FCSTD DOCUMENT  (FreeCAD 0.19R19093 (Git))
Label: switchplate
License: All rights reserved
LicenseURL: http://en.wikipedia.org/wiki/All_rights_reserved
objects: Sketcher::SketchObject×1
note: 1 computed .brp shape members not serialized (recipe doc carries the construction recipe); baked Part::Feature solids carry a one-line shape summary decoded from their .brp

FEATURE [Sketcher::SketchObject] Sketch
  sketch-geometry (1004):
    g0: LineSegment [constr] StartX=-133.598 StartY=68.4339 StartZ=0 EndX=-114.548 EndY=68.4339 EndZ=0
    g1: LineSegment [constr] StartX=-114.548 StartY=68.4339 StartZ=0 EndX=-114.548 EndY=49.3839 EndZ=0
    g2: LineSegment [constr] StartX=-114.548 StartY=49.3839 StartZ=0 EndX=-133.598 EndY=49.3839 EndZ=0
    g3: LineSegment [constr] StartX=-133.598 StartY=49.3839 StartZ=0 EndX=-133.598 EndY=68.4339 EndZ=0
    g4: LineSegment [constr] StartX=-128.836 StartY=68.4339 StartZ=0 EndX=-128.836 EndY=49.3839 EndZ=0
    g5: LineSegment [constr] StartX=-124.073 StartY=68.4339 StartZ=0 EndX=-124.073 EndY=49.3839 EndZ=0
    g6: LineSegment [constr] StartX=-119.311 StartY=68.4339 StartZ=0 EndX=-119.311 EndY=49.3839 EndZ=0
    g7: LineSegment StartX=-131.073 StartY=65.9089 StartZ=0 EndX=-117.073 EndY=65.9089 EndZ=0
    g8: LineSegment StartX=-117.073 StartY=65.9089 StartZ=0 EndX=-117.073 EndY=51.9089 EndZ=0
    g9: LineSegment StartX=-117.073 StartY=51.9089 StartZ=0 EndX=-131.073 EndY=51.9089 EndZ=0
    g10: LineSegment StartX=-131.073 StartY=51.9089 StartZ=0 EndX=-131.073 EndY=65.9089 EndZ=0
    g11: LineSegment [constr] StartX=-129.78 StartY=36.1937 StartZ=0 EndX=-110.73 EndY=36.1937 EndZ=0
    g12: LineSegment [constr] StartX=-110.73 StartY=36.1937 StartZ=0 EndX=-110.73 EndY=17.1437 EndZ=0
    g13: LineSegment [constr] StartX=-110.73 StartY=17.1437 StartZ=0 EndX=-129.78 EndY=17.1437 EndZ=0
    g14: LineSegment [constr] StartX=-129.78 StartY=17.1437 StartZ=0 EndX=-129.78 EndY=36.1937 EndZ=0
    g15: LineSegment [constr] StartX=-125.018 StartY=36.1937 StartZ=0 EndX=-125.018 EndY=17.1437 EndZ=0
    g16: LineSegment [constr] StartX=-120.255 StartY=36.1937 StartZ=0 EndX=-120.255 EndY=17.1437 EndZ=0
    g17: LineSegment [constr] StartX=-115.493 StartY=36.1937 StartZ=0 EndX=-115.493 EndY=17.1437 EndZ=0
    g18: LineSegment [constr] StartX=-110.73 StartY=36.1937 StartZ=0 EndX=-105.968 EndY=36.1937 EndZ=0
    g19: LineSegment [constr] StartX=-105.968 StartY=36.1937 StartZ=0 EndX=-105.968 EndY=17.1437 EndZ=0
    g20: LineSegment [constr] StartX=-105.968 StartY=17.1437 StartZ=0 EndX=-110.73 EndY=17.1437 EndZ=0
    g21: LineSegment [constr] StartX=-117.874 StartY=36.1937 StartZ=0 EndX=-117.874 EndY=17.1437 EndZ=0
    g22: LineSegment StartX=-124.874 StartY=33.6687 StartZ=0 EndX=-110.874 EndY=33.6687 EndZ=0
    g23: LineSegment StartX=-110.874 StartY=33.6687 StartZ=0 EndX=-110.874 EndY=19.6687 EndZ=0
    g24: LineSegment StartX=-110.874 StartY=19.6687 StartZ=0 EndX=-124.874 EndY=19.6687 EndZ=0
    g25: LineSegment StartX=-124.874 StartY=19.6687 StartZ=0 EndX=-124.874 EndY=33.6687 EndZ=0
    g26: GeomPoint X=-117.874 Y=33.6687 Z=0
    g27: LineSegment [constr] StartX=-130.97 StartY=2.89697 StartZ=0 EndX=-111.92 EndY=2.89697 EndZ=0
    g28: LineSegment [constr] StartX=-111.92 StartY=2.89697 StartZ=0 EndX=-111.92 EndY=-16.153 EndZ=0
    g29: LineSegment [constr] StartX=-111.92 StartY=-16.153 StartZ=0 EndX=-130.97 EndY=-16.153 EndZ=0
    g30: LineSegment [constr] StartX=-130.97 StartY=-16.153 StartZ=0 EndX=-130.97 EndY=2.89697 EndZ=0
    g31: LineSegment [constr] StartX=-126.208 StartY=2.89697 StartZ=0 EndX=-126.208 EndY=-16.153 EndZ=0
    g32: LineSegment [constr] StartX=-121.445 StartY=2.89697 StartZ=0 EndX=-121.445 EndY=-16.153 EndZ=0
    g33: LineSegment [constr] StartX=-116.683 StartY=2.89697 StartZ=0 EndX=-116.683 EndY=-16.153 EndZ=0
    g34: LineSegment [constr] StartX=-111.92 StartY=2.89697 StartZ=0 EndX=-107.158 EndY=2.89697 EndZ=0
    g35: LineSegment [constr] StartX=-107.158 StartY=2.89697 StartZ=0 EndX=-107.158 EndY=-16.153 EndZ=0
    g36: LineSegment [constr] StartX=-107.158 StartY=-16.153 StartZ=0 EndX=-111.92 EndY=-16.153 EndZ=0
    g37: LineSegment [constr] StartX=-107.158 StartY=2.89697 StartZ=0 EndX=-102.395 EndY=2.89697 EndZ=0
    g38: LineSegment [constr] StartX=-102.395 StartY=2.89697 StartZ=0 EndX=-102.395 EndY=-16.153 EndZ=0
    g39: LineSegment [constr] StartX=-102.395 StartY=-16.153 StartZ=0 EndX=-107.158 EndY=-16.153 EndZ=0
    g40: LineSegment StartX=-123.683 StartY=0.371972 StartZ=0 EndX=-109.683 EndY=0.371972 EndZ=0
    g41: LineSegment StartX=-109.683 StartY=0.371972 StartZ=0 EndX=-109.683 EndY=-13.628 EndZ=0
    g42: LineSegment StartX=-109.683 StartY=-13.628 StartZ=0 EndX=-123.683 EndY=-13.628 EndZ=0
    g43: LineSegment StartX=-123.683 StartY=-13.628 StartZ=0 EndX=-123.683 EndY=0.371972 EndZ=0
    g44: GeomPoint X=-116.683 Y=0.371972 Z=0
    g45: LineSegment [constr] StartX=-131.666 StartY=-25.3858 StartZ=0 EndX=-112.616 EndY=-25.3858 EndZ=0
    g46: LineSegment [constr] StartX=-112.616 StartY=-25.3858 StartZ=0 EndX=-112.616 EndY=-44.4358 EndZ=0
    g47: LineSegment [constr] StartX=-112.616 StartY=-44.4358 StartZ=0 EndX=-131.666 EndY=-44.4358 EndZ=0
    g48: LineSegment [constr] StartX=-131.666 StartY=-44.4358 StartZ=0 EndX=-131.666 EndY=-25.3858 EndZ=0
    g49: LineSegment [constr] StartX=-126.903 StartY=-25.3858 StartZ=0 EndX=-126.903 EndY=-44.4358 EndZ=0
    g50: LineSegment [constr] StartX=-122.141 StartY=-25.3858 StartZ=0 EndX=-122.141 EndY=-44.4358 EndZ=0
    g51: LineSegment [constr] StartX=-117.378 StartY=-25.3858 StartZ=0 EndX=-117.378 EndY=-44.4358 EndZ=0
    g52: LineSegment [constr] StartX=-112.616 StartY=-25.3858 StartZ=0 EndX=-107.853 EndY=-25.3858 EndZ=0
    g53: LineSegment [constr] StartX=-107.853 StartY=-25.3858 StartZ=0 EndX=-107.853 EndY=-44.4358 EndZ=0
    g54: LineSegment [constr] StartX=-107.853 StartY=-44.4358 StartZ=0 EndX=-112.616 EndY=-44.4358 EndZ=0
    g55: LineSegment [constr] StartX=-107.853 StartY=-25.3858 StartZ=0 EndX=-103.091 EndY=-25.3858 EndZ=0
    g56: LineSegment [constr] StartX=-103.091 StartY=-25.3858 StartZ=0 EndX=-103.091 EndY=-44.4358 EndZ=0
    g57: LineSegment [constr] StartX=-103.091 StartY=-44.4358 StartZ=0 EndX=-107.853 EndY=-44.4358 EndZ=0
    g58: LineSegment [constr] StartX=-103.091 StartY=-25.3858 StartZ=0 EndX=-98.3281 EndY=-25.3858 EndZ=0
    g59: LineSegment [constr] StartX=-98.3281 StartY=-25.3858 StartZ=0 EndX=-98.3281 EndY=-44.4358 EndZ=0
    g60: LineSegment [constr] StartX=-98.3281 StartY=-44.4358 StartZ=0 EndX=-103.091 EndY=-44.4358 EndZ=0
    g61: LineSegment [constr] StartX=-114.997 StartY=-25.3858 StartZ=0 EndX=-114.997 EndY=-44.4358 EndZ=0
    g62: LineSegment StartX=-121.997 StartY=-27.9108 StartZ=0 EndX=-107.997 EndY=-27.9108 EndZ=0
    g63: LineSegment StartX=-107.997 StartY=-27.9108 StartZ=0 EndX=-107.997 EndY=-41.9108 EndZ=0
    g64: LineSegment StartX=-107.997 StartY=-41.9108 StartZ=0 EndX=-121.997 EndY=-41.9108 EndZ=0
    g65: LineSegment StartX=-121.997 StartY=-41.9108 StartZ=0 EndX=-121.997 EndY=-27.9108 EndZ=0
    g66: GeomPoint X=-114.997 Y=-27.9108 Z=0
    g67: LineSegment [constr] StartX=-133.994 StartY=-54.7146 StartZ=0 EndX=-114.944 EndY=-54.7146 EndZ=0
    g68: LineSegment [constr] StartX=-114.944 StartY=-54.7146 StartZ=0 EndX=-114.944 EndY=-73.7646 EndZ=0
    g69: LineSegment [constr] StartX=-114.944 StartY=-73.7646 StartZ=0 EndX=-133.994 EndY=-73.7646 EndZ=0
    g70: LineSegment [constr] StartX=-133.994 StartY=-73.7646 StartZ=0 EndX=-133.994 EndY=-54.7146 EndZ=0
    g71: LineSegment [constr] StartX=-129.232 StartY=-54.7146 StartZ=0 EndX=-129.232 EndY=-73.7646 EndZ=0
    g72: LineSegment [constr] StartX=-124.469 StartY=-54.7146 StartZ=0 EndX=-124.469 EndY=-73.7646 EndZ=0
    g73: LineSegment [constr] StartX=-119.707 StartY=-54.7146 StartZ=0 EndX=-119.707 EndY=-73.7646 EndZ=0
    g74: LineSegment [constr] StartX=-114.944 StartY=-54.7146 StartZ=0 EndX=-110.182 EndY=-54.7146 EndZ=0
    g75: LineSegment [constr] StartX=-110.182 StartY=-54.7146 StartZ=0 EndX=-110.182 EndY=-73.7646 EndZ=0
    g76: LineSegment [constr] StartX=-110.182 StartY=-73.7646 StartZ=0 EndX=-114.944 EndY=-73.7646 EndZ=0
    g77: LineSegment [constr] StartX=-110.182 StartY=-54.7146 StartZ=0 EndX=-105.419 EndY=-54.7146 EndZ=0
    g78: LineSegment [constr] StartX=-105.419 StartY=-54.7146 StartZ=0 EndX=-105.419 EndY=-73.7646 EndZ=0
    g79: LineSegment [constr] StartX=-105.419 StartY=-73.7646 StartZ=0 EndX=-110.182 EndY=-73.7646 EndZ=0
    g80: LineSegment [constr] StartX=-105.419 StartY=-54.7146 StartZ=0 EndX=-100.657 EndY=-54.7146 EndZ=0
    g81: LineSegment [constr] StartX=-100.657 StartY=-54.7146 StartZ=0 EndX=-100.657 EndY=-73.7646 EndZ=0
    g82: LineSegment [constr] StartX=-100.657 StartY=-73.7646 StartZ=0 EndX=-105.419 EndY=-73.7646 EndZ=0
    g83: LineSegment [constr] StartX=-100.657 StartY=-54.7146 StartZ=0 EndX=-95.8941 EndY=-54.7146 EndZ=0
    g84: LineSegment [constr] StartX=-95.8941 StartY=-54.7146 StartZ=0 EndX=-95.8941 EndY=-73.7646 EndZ=0
    g85: LineSegment [constr] StartX=-95.8941 StartY=-73.7646 StartZ=0 EndX=-100.657 EndY=-73.7646 EndZ=0
    g86: LineSegment StartX=-121.944 StartY=-57.2396 StartZ=0 EndX=-107.944 EndY=-57.2396 EndZ=0
    g87: LineSegment StartX=-107.944 StartY=-57.2396 StartZ=0 EndX=-107.944 EndY=-71.2396 EndZ=0
    g88: LineSegment StartX=-107.944 StartY=-71.2396 StartZ=0 EndX=-121.944 EndY=-71.2396 EndZ=0
    g89: LineSegment StartX=-121.944 StartY=-71.2396 StartZ=0 EndX=-121.944 EndY=-57.2396 EndZ=0
    g90: GeomPoint X=-114.944 Y=-57.2396 Z=0
    g91: LineSegment [constr] StartX=-133.693 StartY=-86.5988 StartZ=0 EndX=-114.643 EndY=-86.5988 EndZ=0
    g92: LineSegment [constr] StartX=-114.643 StartY=-86.5988 StartZ=0 EndX=-114.643 EndY=-105.649 EndZ=0
    g93: LineSegment [constr] StartX=-114.643 StartY=-105.649 StartZ=0 EndX=-133.693 EndY=-105.649 EndZ=0
    g94: LineSegment [constr] StartX=-133.693 StartY=-105.649 StartZ=0 EndX=-133.693 EndY=-86.5988 EndZ=0
    g95: LineSegment [constr] StartX=-128.93 StartY=-86.5988 StartZ=0 EndX=-128.93 EndY=-105.649 EndZ=0
    g96: LineSegment [constr] StartX=-124.168 StartY=-86.5988 StartZ=0 EndX=-124.168 EndY=-105.649 EndZ=0
    g97: LineSegment [constr] StartX=-119.405 StartY=-86.5988 StartZ=0 EndX=-119.405 EndY=-105.649 EndZ=0
    g98: LineSegment [constr] StartX=-114.643 StartY=-86.5988 StartZ=0 EndX=-109.88 EndY=-86.5988 EndZ=0
    g99: LineSegment [constr] StartX=-109.88 StartY=-86.5988 StartZ=0 EndX=-109.88 EndY=-105.649 EndZ=0
    g100: LineSegment [constr] StartX=-109.88 StartY=-105.649 StartZ=0 EndX=-114.643 EndY=-105.649 EndZ=0
    g101: LineSegment [constr] StartX=-109.88 StartY=-86.5988 StartZ=0 EndX=-105.118 EndY=-86.5988 EndZ=0
    g102: LineSegment [constr] StartX=-105.118 StartY=-86.5988 StartZ=0 EndX=-105.118 EndY=-105.649 EndZ=0
    g103: LineSegment [constr] StartX=-105.118 StartY=-105.649 StartZ=0 EndX=-109.88 EndY=-105.649 EndZ=0
    g104: LineSegment [constr] StartX=-105.118 StartY=-86.5988 StartZ=0 EndX=-100.355 EndY=-86.5988 EndZ=0
    g105: LineSegment [constr] StartX=-100.355 StartY=-86.5988 StartZ=0 EndX=-100.355 EndY=-105.649 EndZ=0
    g106: LineSegment [constr] StartX=-100.355 StartY=-105.649 StartZ=0 EndX=-105.118 EndY=-105.649 EndZ=0
    g107: LineSegment [constr] StartX=-100.355 StartY=-86.5988 StartZ=0 EndX=-95.5928 EndY=-86.5988 EndZ=0
    g108: LineSegment [constr] StartX=-95.5928 StartY=-86.5988 StartZ=0 EndX=-95.5928 EndY=-105.649 EndZ=0
    g109: LineSegment [constr] StartX=-95.5928 StartY=-105.649 StartZ=0 EndX=-100.355 EndY=-105.649 EndZ=0
    g110: LineSegment [constr] StartX=-95.5928 StartY=-86.5988 StartZ=0 EndX=-90.8303 EndY=-86.5988 EndZ=0
    g111: LineSegment [constr] StartX=-90.8303 StartY=-86.5988 StartZ=0 EndX=-90.8303 EndY=-105.649 EndZ=0
    g112: LineSegment [constr] StartX=-90.8303 StartY=-105.649 StartZ=0 EndX=-95.5928 EndY=-105.649 EndZ=0
    g113: LineSegment [constr] StartX=-112.262 StartY=-86.5988 StartZ=0 EndX=-112.262 EndY=-105.649 EndZ=0
    g114: GeomPoint X=-112.262 Y=-89.1238 Z=0
    g115: LineSegment StartX=-119.262 StartY=-89.1238 StartZ=0 EndX=-105.262 EndY=-89.1238 EndZ=0
    g116: LineSegment StartX=-105.262 StartY=-89.1238 StartZ=0 EndX=-105.262 EndY=-103.124 EndZ=0
    g117: LineSegment StartX=-105.262 StartY=-103.124 StartZ=0 EndX=-119.262 EndY=-103.124 EndZ=0
    g118: LineSegment StartX=-119.262 StartY=-103.124 StartZ=0 EndX=-119.262 EndY=-89.1238 EndZ=0
    g119: LineSegment [constr] StartX=-64.4313 StartY=98.9607 StartZ=0 EndX=-45.3813 EndY=98.9607 EndZ=0
    g120: LineSegment [constr] StartX=-45.3813 StartY=98.9607 StartZ=0 EndX=-45.3813 EndY=79.9107 EndZ=0
    g121: LineSegment [constr] StartX=-45.3813 StartY=79.9107 StartZ=0 EndX=-64.4313 EndY=79.9107 EndZ=0
    g122: LineSegment [constr] StartX=-64.4313 StartY=79.9107 StartZ=0 EndX=-64.4313 EndY=98.9607 EndZ=0
    g123: LineSegment [constr] StartX=-59.6688 StartY=98.9607 StartZ=0 EndX=-59.6688 EndY=79.9107 EndZ=0
    g124: LineSegment [constr] StartX=-54.9063 StartY=98.9607 StartZ=0 EndX=-54.9063 EndY=79.9107 EndZ=0
    g125: LineSegment [constr] StartX=-50.1438 StartY=98.9607 StartZ=0 EndX=-50.1438 EndY=79.9107 EndZ=0
    g126: LineSegment StartX=-61.9063 StartY=96.4357 StartZ=0 EndX=-47.9063 EndY=96.4357 EndZ=0
    g127: LineSegment StartX=-47.9063 StartY=96.4357 StartZ=0 EndX=-47.9063 EndY=82.4357 EndZ=0
    g128: LineSegment StartX=-47.9063 StartY=82.4357 StartZ=0 EndX=-61.9063 EndY=82.4357 EndZ=0
    g129: LineSegment StartX=-61.9063 StartY=82.4357 StartZ=0 EndX=-61.9063 EndY=96.4357 EndZ=0
    g130: LineSegment [constr] StartX=-35.8563 StartY=98.9607 StartZ=0 EndX=-16.8063 EndY=98.9607 EndZ=0
    g131: LineSegment [constr] StartX=-16.8063 StartY=98.9607 StartZ=0 EndX=-16.8063 EndY=79.9107 EndZ=0
    g132: LineSegment [constr] StartX=-16.8063 StartY=79.9107 StartZ=0 EndX=-35.8563 EndY=79.9107 EndZ=0
    g133: LineSegment [constr] StartX=-35.8563 StartY=79.9107 StartZ=0 EndX=-35.8563 EndY=98.9607 EndZ=0
    g134: LineSegment [constr] StartX=-31.0938 StartY=98.9607 StartZ=0 EndX=-31.0938 EndY=79.9107 EndZ=0
    g135: LineSegment [constr] StartX=-26.3313 StartY=98.9607 StartZ=0 EndX=-26.3313 EndY=79.9107 EndZ=0
    g136: LineSegment [constr] StartX=-21.5688 StartY=98.9607 StartZ=0 EndX=-21.5688 EndY=79.9107 EndZ=0
    g137: LineSegment StartX=-33.3313 StartY=96.4357 StartZ=0 EndX=-19.3313 EndY=96.4357 EndZ=0
    g138: LineSegment StartX=-19.3313 StartY=96.4357 StartZ=0 EndX=-19.3313 EndY=82.4357 EndZ=0
    g139: LineSegment StartX=-19.3313 StartY=82.4357 StartZ=0 EndX=-33.3313 EndY=82.4357 EndZ=0
    g140: LineSegment StartX=-33.3313 StartY=82.4357 StartZ=0 EndX=-33.3313 EndY=96.4357 EndZ=0
    g141: LineSegment [constr] StartX=-16.8063 StartY=98.9607 StartZ=0 EndX=2.24369 EndY=98.9607 EndZ=0
    g142: LineSegment [constr] StartX=2.24369 StartY=98.9607 StartZ=0 EndX=2.24369 EndY=79.9107 EndZ=0
    g143: LineSegment [constr] StartX=2.24369 StartY=79.9107 StartZ=0 EndX=-16.8063 EndY=79.9107 EndZ=0
    g144: LineSegment [constr] StartX=-16.8063 StartY=79.9107 StartZ=0 EndX=-16.8063 EndY=98.9607 EndZ=0
    g145: LineSegment [constr] StartX=-12.0438 StartY=98.9607 StartZ=0 EndX=-12.0438 EndY=79.9107 EndZ=0
    g146: LineSegment [constr] StartX=-7.28131 StartY=98.9607 StartZ=0 EndX=-7.28131 EndY=79.9107 EndZ=0
    g147: LineSegment [constr] StartX=-2.51881 StartY=98.9607 StartZ=0 EndX=-2.51881 EndY=79.9107 EndZ=0
    g148: LineSegment StartX=-14.2813 StartY=96.4357 StartZ=0 EndX=-0.28131 EndY=96.4357 EndZ=0
    g149: LineSegment StartX=-0.28131 StartY=96.4357 StartZ=0 EndX=-0.28131 EndY=82.4357 EndZ=0
    g150: LineSegment StartX=-0.28131 StartY=82.4357 StartZ=0 EndX=-14.2813 EndY=82.4357 EndZ=0
    g151: LineSegment StartX=-14.2813 StartY=82.4357 StartZ=0 EndX=-14.2813 EndY=96.4357 EndZ=0
    g152: LineSegment [constr] StartX=2.24369 StartY=98.9607 StartZ=0 EndX=21.2937 EndY=98.9607 EndZ=0
    g153: LineSegment [constr] StartX=21.2937 StartY=98.9607 StartZ=0 EndX=21.2937 EndY=79.9107 EndZ=0
    g154: LineSegment [constr] StartX=21.2937 StartY=79.9107 StartZ=0 EndX=2.24369 EndY=79.9107 EndZ=0
    g155: LineSegment [constr] StartX=2.24369 StartY=79.9107 StartZ=0 EndX=2.24369 EndY=98.9607 EndZ=0
    g156: LineSegment [constr] StartX=7.00619 StartY=98.9607 StartZ=0 EndX=7.00619 EndY=79.9107 EndZ=0
    g157: LineSegment [constr] StartX=11.7687 StartY=98.9607 StartZ=0 EndX=11.7687 EndY=79.9107 EndZ=0
    g158: LineSegment [constr] StartX=16.5312 StartY=98.9607 StartZ=0 EndX=16.5312 EndY=79.9107 EndZ=0
    g159: LineSegment StartX=4.76869 StartY=96.4357 StartZ=0 EndX=18.7687 EndY=96.4357 EndZ=0
    g160: LineSegment StartX=18.7687 StartY=96.4357 StartZ=0 EndX=18.7687 EndY=82.4357 EndZ=0
    g161: LineSegment StartX=18.7687 StartY=82.4357 StartZ=0 EndX=4.76869 EndY=82.4357 EndZ=0
    g162: LineSegment StartX=4.76869 StartY=82.4357 StartZ=0 EndX=4.76869 EndY=96.4357 EndZ=0
    g163: LineSegment [constr] StartX=21.2937 StartY=98.9607 StartZ=0 EndX=40.3437 EndY=98.9607 EndZ=0
    g164: LineSegment [constr] StartX=40.3437 StartY=98.9607 StartZ=0 EndX=40.3437 EndY=79.9107 EndZ=0
    g165: LineSegment [constr] StartX=40.3437 StartY=79.9107 StartZ=0 EndX=21.2937 EndY=79.9107 EndZ=0
    g166: LineSegment [constr] StartX=21.2937 StartY=79.9107 StartZ=0 EndX=21.2937 EndY=98.9607 EndZ=0
    g167: LineSegment [constr] StartX=26.0562 StartY=98.9607 StartZ=0 EndX=26.0562 EndY=79.9107 EndZ=0
    g168: LineSegment [constr] StartX=30.8187 StartY=98.9607 StartZ=0 EndX=30.8187 EndY=79.9107 EndZ=0
    g169: LineSegment [constr] StartX=35.5812 StartY=98.9607 StartZ=0 EndX=35.5812 EndY=79.9107 EndZ=0
    g170: LineSegment StartX=23.8187 StartY=96.4357 StartZ=0 EndX=37.8187 EndY=96.4357 EndZ=0
    g171: LineSegment StartX=37.8187 StartY=96.4357 StartZ=0 EndX=37.8187 EndY=82.4357 EndZ=0
    g172: LineSegment StartX=37.8187 StartY=82.4357 StartZ=0 EndX=23.8187 EndY=82.4357 EndZ=0
    g173: LineSegment StartX=23.8187 StartY=82.4357 StartZ=0 EndX=23.8187 EndY=96.4357 EndZ=0
    g174: LineSegment [constr] StartX=54.6312 StartY=98.9607 StartZ=0 EndX=73.6812 EndY=98.9607 EndZ=0
    g175: LineSegment [constr] StartX=73.6812 StartY=98.9607 StartZ=0 EndX=73.6812 EndY=79.9107 EndZ=0
    g176: LineSegment [constr] StartX=73.6812 StartY=79.9107 StartZ=0 EndX=54.6312 EndY=79.9107 EndZ=0
    g177: LineSegment [constr] StartX=54.6312 StartY=79.9107 StartZ=0 EndX=54.6312 EndY=98.9607 EndZ=0
    g178: LineSegment [constr] StartX=59.3937 StartY=98.9607 StartZ=0 EndX=59.3937 EndY=79.9107 EndZ=0
    g179: LineSegment [constr] StartX=64.1562 StartY=98.9607 StartZ=0 EndX=64.1562 EndY=79.9107 EndZ=0
    g180: LineSegment [constr] StartX=68.9187 StartY=98.9607 StartZ=0 EndX=68.9187 EndY=79.9107 EndZ=0
    g181: LineSegment StartX=57.1562 StartY=96.4357 StartZ=0 EndX=71.1562 EndY=96.4357 EndZ=0
    g182: LineSegment StartX=71.1562 StartY=96.4357 StartZ=0 EndX=71.1562 EndY=82.4357 EndZ=0
    g183: LineSegment StartX=71.1562 StartY=82.4357 StartZ=0 EndX=57.1562 EndY=82.4357 EndZ=0
    g184: LineSegment StartX=57.1562 StartY=82.4357 StartZ=0 EndX=57.1562 EndY=96.4357 EndZ=0
    g185: LineSegment [constr] StartX=73.6812 StartY=98.9607 StartZ=0 EndX=92.7312 EndY=98.9607 EndZ=0
    g186: LineSegment [constr] StartX=92.7312 StartY=98.9607 StartZ=0 EndX=92.7312 EndY=79.9107 EndZ=0
    g187: LineSegment [constr] StartX=92.7312 StartY=79.9107 StartZ=0 EndX=73.6812 EndY=79.9107 EndZ=0
    g188: LineSegment [constr] StartX=73.6812 StartY=79.9107 StartZ=0 EndX=73.6812 EndY=98.9607 EndZ=0
    g189: LineSegment [constr] StartX=78.4437 StartY=98.9607 StartZ=0 EndX=78.4437 EndY=79.9107 EndZ=0
    g190: LineSegment [constr] StartX=83.2062 StartY=98.9607 StartZ=0 EndX=83.2062 EndY=79.9107 EndZ=0
    g191: LineSegment [constr] StartX=87.9687 StartY=98.9607 StartZ=0 EndX=87.9687 EndY=79.9107 EndZ=0
    g192: LineSegment StartX=76.2062 StartY=96.4357 StartZ=0 EndX=90.2062 EndY=96.4357 EndZ=0
    g193: LineSegment StartX=90.2062 StartY=96.4357 StartZ=0 EndX=90.2062 EndY=82.4357 EndZ=0
    g194: LineSegment StartX=90.2062 StartY=82.4357 StartZ=0 EndX=76.2062 EndY=82.4357 EndZ=0
    g195: LineSegment StartX=76.2062 StartY=82.4357 StartZ=0 EndX=76.2062 EndY=96.4357 EndZ=0
    g196: LineSegment [constr] StartX=92.7312 StartY=98.9607 StartZ=0 EndX=111.781 EndY=98.9607 EndZ=0
    g197: LineSegment [constr] StartX=111.781 StartY=98.9607 StartZ=0 EndX=111.781 EndY=79.9107 EndZ=0
    g198: LineSegment [constr] StartX=111.781 StartY=79.9107 StartZ=0 EndX=92.7312 EndY=79.9107 EndZ=0
    g199: LineSegment [constr] StartX=92.7312 StartY=79.9107 StartZ=0 EndX=92.7312 EndY=98.9607 EndZ=0
    g200: LineSegment [constr] StartX=97.4937 StartY=98.9607 StartZ=0 EndX=97.4937 EndY=79.9107 EndZ=0
    g201: LineSegment [constr] StartX=102.256 StartY=98.9607 StartZ=0 EndX=102.256 EndY=79.9107 EndZ=0
    g202: LineSegment [constr] StartX=107.019 StartY=98.9607 StartZ=0 EndX=107.019 EndY=79.9107 EndZ=0
    g203: LineSegment StartX=95.2562 StartY=96.4357 StartZ=0 EndX=109.256 EndY=96.4357 EndZ=0
    g204: LineSegment StartX=109.256 StartY=96.4357 StartZ=0 EndX=109.256 EndY=82.4357 EndZ=0
    g205: LineSegment StartX=109.256 StartY=82.4357 StartZ=0 EndX=95.2562 EndY=82.4357 EndZ=0
    g206: LineSegment StartX=95.2562 StartY=82.4357 StartZ=0 EndX=95.2562 EndY=96.4357 EndZ=0
    g207: LineSegment [constr] StartX=111.781 StartY=98.9607 StartZ=0 EndX=130.831 EndY=98.9607 EndZ=0
    g208: LineSegment [constr] StartX=130.831 StartY=98.9607 StartZ=0 EndX=130.831 EndY=79.9107 EndZ=0
    g209: LineSegment [constr] StartX=130.831 StartY=79.9107 StartZ=0 EndX=111.781 EndY=79.9107 EndZ=0
    g210: LineSegment [constr] StartX=111.781 StartY=79.9107 StartZ=0 EndX=111.781 EndY=98.9607 EndZ=0
    g211: LineSegment [constr] StartX=116.544 StartY=98.9607 StartZ=0 EndX=116.544 EndY=79.9107 EndZ=0
    g212: LineSegment [constr] StartX=121.306 StartY=98.9607 StartZ=0 EndX=121.306 EndY=79.9107 EndZ=0
    g213: LineSegment [constr] StartX=126.069 StartY=98.9607 StartZ=0 EndX=126.069 EndY=79.9107 EndZ=0
    g214: LineSegment StartX=114.306 StartY=96.4357 StartZ=0 EndX=128.306 EndY=96.4357 EndZ=0
    g215: LineSegment StartX=128.306 StartY=96.4357 StartZ=0 EndX=128.306 EndY=82.4357 EndZ=0
    g216: LineSegment StartX=128.306 StartY=82.4357 StartZ=0 EndX=114.306 EndY=82.4357 EndZ=0
    g217: LineSegment StartX=114.306 StartY=82.4357 StartZ=0 EndX=114.306 EndY=96.4357 EndZ=0
    g218: LineSegment [constr] StartX=145.119 StartY=98.9607 StartZ=0 EndX=164.169 EndY=98.9607 EndZ=0
    g219: LineSegment [constr] StartX=164.169 StartY=98.9607 StartZ=0 EndX=164.169 EndY=79.9107 EndZ=0
    g220: LineSegment [constr] StartX=164.169 StartY=79.9107 StartZ=0 EndX=145.119 EndY=79.9107 EndZ=0
    g221: LineSegment [constr] StartX=145.119 StartY=79.9107 StartZ=0 EndX=145.119 EndY=98.9607 EndZ=0
    g222: LineSegment [constr] StartX=149.881 StartY=98.9607 StartZ=0 EndX=149.881 EndY=79.9107 EndZ=0
    g223: LineSegment [constr] StartX=154.644 StartY=98.9607 StartZ=0 EndX=154.644 EndY=79.9107 EndZ=0
    g224: LineSegment [constr] StartX=159.406 StartY=98.9607 StartZ=0 EndX=159.406 EndY=79.9107 EndZ=0
    g225: LineSegment StartX=147.644 StartY=96.4357 StartZ=0 EndX=161.644 EndY=96.4357 EndZ=0
    g226: LineSegment StartX=161.644 StartY=96.4357 StartZ=0 EndX=161.644 EndY=82.4357 EndZ=0
    g227: LineSegment StartX=161.644 StartY=82.4357 StartZ=0 EndX=147.644 EndY=82.4357 EndZ=0
    g228: LineSegment StartX=147.644 StartY=82.4357 StartZ=0 EndX=147.644 EndY=96.4357 EndZ=0
    g229: LineSegment [constr] StartX=164.169 StartY=98.9607 StartZ=0 EndX=183.219 EndY=98.9607 EndZ=0
    g230: LineSegment [constr] StartX=183.219 StartY=98.9607 StartZ=0 EndX=183.219 EndY=79.9107 EndZ=0
    g231: LineSegment [constr] StartX=183.219 StartY=79.9107 StartZ=0 EndX=164.169 EndY=79.9107 EndZ=0
    g232: LineSegment [constr] StartX=164.169 StartY=79.9107 StartZ=0 EndX=164.169 EndY=98.9607 EndZ=0
    g233: LineSegment [constr] StartX=168.931 StartY=98.9607 StartZ=0 EndX=168.931 EndY=79.9107 EndZ=0
    g234: LineSegment [constr] StartX=173.694 StartY=98.9607 StartZ=0 EndX=173.694 EndY=79.9107 EndZ=0
    g235: LineSegment [constr] StartX=178.456 StartY=98.9607 StartZ=0 EndX=178.456 EndY=79.9107 EndZ=0
    g236: LineSegment StartX=166.694 StartY=96.4357 StartZ=0 EndX=180.694 EndY=96.4357 EndZ=0
    g237: LineSegment StartX=180.694 StartY=96.4357 StartZ=0 EndX=180.694 EndY=82.4357 EndZ=0
    g238: LineSegment StartX=180.694 StartY=82.4357 StartZ=0 EndX=166.694 EndY=82.4357 EndZ=0
    g239: LineSegment StartX=166.694 StartY=82.4357 StartZ=0 EndX=166.694 EndY=96.4357 EndZ=0
    g240: LineSegment [constr] StartX=183.219 StartY=98.9607 StartZ=0 EndX=202.269 EndY=98.9607 EndZ=0
    g241: LineSegment [constr] StartX=202.269 StartY=98.9607 StartZ=0 EndX=202.269 EndY=79.9107 EndZ=0
    g242: LineSegment [constr] StartX=202.269 StartY=79.9107 StartZ=0 EndX=183.219 EndY=79.9107 EndZ=0
    g243: LineSegment [constr] StartX=183.219 StartY=79.9107 StartZ=0 EndX=183.219 EndY=98.9607 EndZ=0
    g244: LineSegment [constr] StartX=187.981 StartY=98.9607 StartZ=0 EndX=187.981 EndY=79.9107 EndZ=0
    g245: LineSegment [constr] StartX=192.744 StartY=98.9607 StartZ=0 EndX=192.744 EndY=79.9107 EndZ=0
    g246: LineSegment [constr] StartX=197.506 StartY=98.9607 StartZ=0 EndX=197.506 EndY=79.9107 EndZ=0
    g247: LineSegment StartX=185.744 StartY=96.4357 StartZ=0 EndX=199.744 EndY=96.4357 EndZ=0
    g248: LineSegment StartX=199.744 StartY=96.4357 StartZ=0 EndX=199.744 EndY=82.4357 EndZ=0
    g249: LineSegment StartX=199.744 StartY=82.4357 StartZ=0 EndX=185.744 EndY=82.4357 EndZ=0
    g250: LineSegment StartX=185.744 StartY=82.4357 StartZ=0 EndX=185.744 EndY=96.4357 EndZ=0
    g251: LineSegment [constr] StartX=202.269 StartY=98.9607 StartZ=0 EndX=221.319 EndY=98.9607 EndZ=0
    g252: LineSegment [constr] StartX=221.319 StartY=98.9607 StartZ=0 EndX=221.319 EndY=79.9107 EndZ=0
    g253: LineSegment [constr] StartX=221.319 StartY=79.9107 StartZ=0 EndX=202.269 EndY=79.9107 EndZ=0
    g254: LineSegment [constr] StartX=202.269 StartY=79.9107 StartZ=0 EndX=202.269 EndY=98.9607 EndZ=0
    g255: LineSegment [constr] StartX=207.031 StartY=98.9607 StartZ=0 EndX=207.031 EndY=79.9107 EndZ=0
    g256: LineSegment [constr] StartX=211.794 StartY=98.9607 StartZ=0 EndX=211.794 EndY=79.9107 EndZ=0
    g257: LineSegment [constr] StartX=216.556 StartY=98.9607 StartZ=0 EndX=216.556 EndY=79.9107 EndZ=0
    g258: LineSegment StartX=204.794 StartY=96.4357 StartZ=0 EndX=218.794 EndY=96.4357 EndZ=0
    g259: LineSegment StartX=218.794 StartY=96.4357 StartZ=0 EndX=218.794 EndY=82.4357 EndZ=0
    g260: LineSegment StartX=218.794 StartY=82.4357 StartZ=0 EndX=204.794 EndY=82.4357 EndZ=0
    g261: LineSegment StartX=204.794 StartY=82.4357 StartZ=0 EndX=204.794 EndY=96.4357 EndZ=0
    g262: LineSegment [constr] StartX=228.106 StartY=99.0816 StartZ=0 EndX=247.156 EndY=99.0816 EndZ=0
    g263: LineSegment [constr] StartX=247.156 StartY=99.0816 StartZ=0 EndX=247.156 EndY=80.0316 EndZ=0
    g264: LineSegment [constr] StartX=247.156 StartY=80.0316 StartZ=0 EndX=228.106 EndY=80.0316 EndZ=0
    g265: LineSegment [constr] StartX=228.106 StartY=80.0316 StartZ=0 EndX=228.106 EndY=99.0816 EndZ=0
    g266: LineSegment [constr] StartX=232.869 StartY=99.0816 StartZ=0 EndX=232.869 EndY=80.0316 EndZ=0
    g267: LineSegment [constr] StartX=237.631 StartY=99.0816 StartZ=0 EndX=237.631 EndY=80.0316 EndZ=0
    g268: LineSegment [constr] StartX=242.394 StartY=99.0816 StartZ=0 EndX=242.394 EndY=80.0316 EndZ=0
    g269: LineSegment StartX=230.631 StartY=96.5566 StartZ=0 EndX=244.631 EndY=96.5566 EndZ=0
    g270: LineSegment StartX=244.631 StartY=96.5566 StartZ=0 EndX=244.631 EndY=82.5566 EndZ=0
    g271: LineSegment StartX=244.631 StartY=82.5566 StartZ=0 EndX=230.631 EndY=82.5566 EndZ=0
    g272: LineSegment StartX=230.631 StartY=82.5566 StartZ=0 EndX=230.631 EndY=96.5566 EndZ=0
    g273: LineSegment [constr] StartX=228.106 StartY=89.5566 StartZ=0 EndX=247.156 EndY=89.5566 EndZ=0
    g274: GeomPoint X=237.631 Y=89.5566 Z=0
    g275: LineSegment [constr] StartX=-64.4313 StartY=72.7682 StartZ=0 EndX=-45.3813 EndY=72.7682 EndZ=0
    g276: LineSegment [constr] StartX=-45.3813 StartY=72.7682 StartZ=0 EndX=-45.3813 EndY=53.7182 EndZ=0
    g277: LineSegment [constr] StartX=-45.3813 StartY=53.7182 StartZ=0 EndX=-64.4313 EndY=53.7182 EndZ=0
    g278: LineSegment [constr] StartX=-64.4313 StartY=53.7182 StartZ=0 EndX=-64.4313 EndY=72.7682 EndZ=0
    g279: LineSegment [constr] StartX=-59.6688 StartY=72.7682 StartZ=0 EndX=-59.6688 EndY=53.7182 EndZ=0
    g280: LineSegment [constr] StartX=-54.9063 StartY=72.7682 StartZ=0 EndX=-54.9063 EndY=53.7182 EndZ=0
    g281: LineSegment [constr] StartX=-50.1438 StartY=72.7682 StartZ=0 EndX=-50.1438 EndY=53.7182 EndZ=0
    g282: LineSegment StartX=-61.9063 StartY=70.2432 StartZ=0 EndX=-47.9063 EndY=70.2432 EndZ=0
    g283: LineSegment StartX=-47.9063 StartY=70.2432 StartZ=0 EndX=-47.9063 EndY=56.2432 EndZ=0
    g284: LineSegment StartX=-47.9063 StartY=56.2432 StartZ=0 EndX=-61.9063 EndY=56.2432 EndZ=0
    g285: LineSegment StartX=-61.9063 StartY=56.2432 StartZ=0 EndX=-61.9063 EndY=70.2432 EndZ=0
    g286: LineSegment [constr] StartX=-45.3813 StartY=72.7682 StartZ=0 EndX=-26.3313 EndY=72.7682 EndZ=0
    g287: LineSegment [constr] StartX=-26.3313 StartY=72.7682 StartZ=0 EndX=-26.3313 EndY=53.7182 EndZ=0
    g288: LineSegment [constr] StartX=-26.3313 StartY=53.7182 StartZ=0 EndX=-45.3813 EndY=53.7182 EndZ=0
    g289: LineSegment [constr] StartX=-45.3813 StartY=53.7182 StartZ=0 EndX=-45.3813 EndY=72.7682 EndZ=0
    g290: LineSegment [constr] StartX=-40.6188 StartY=72.7682 StartZ=0 EndX=-40.6188 EndY=53.7182 EndZ=0
    g291: LineSegment [constr] StartX=-35.8563 StartY=72.7682 StartZ=0 EndX=-35.8563 EndY=53.7182 EndZ=0
    g292: LineSegment [constr] StartX=-31.0938 StartY=72.7682 StartZ=0 EndX=-31.0938 EndY=53.7182 EndZ=0
    g293: LineSegment StartX=-42.8563 StartY=70.2432 StartZ=0 EndX=-28.8563 EndY=70.2432 EndZ=0
    g294: LineSegment StartX=-28.8563 StartY=70.2432 StartZ=0 EndX=-28.8563 EndY=56.2432 EndZ=0
    g295: LineSegment StartX=-28.8563 StartY=56.2432 StartZ=0 EndX=-42.8563 EndY=56.2432 EndZ=0
    g296: LineSegment StartX=-42.8563 StartY=56.2432 StartZ=0 EndX=-42.8563 EndY=70.2432 EndZ=0
    g297: LineSegment [constr] StartX=-26.3313 StartY=72.7682 StartZ=0 EndX=-7.28131 EndY=72.7682 EndZ=0
    g298: LineSegment [constr] StartX=-7.28131 StartY=72.7682 StartZ=0 EndX=-7.28131 EndY=53.7182 EndZ=0
    g299: LineSegment [constr] StartX=-7.28131 StartY=53.7182 StartZ=0 EndX=-26.3313 EndY=53.7182 EndZ=0
    g300: LineSegment [constr] StartX=-26.3313 StartY=53.7182 StartZ=0 EndX=-26.3313 EndY=72.7682 EndZ=0
    g301: LineSegment [constr] StartX=-21.5688 StartY=72.7682 StartZ=0 EndX=-21.5688 EndY=53.7182 EndZ=0
    g302: LineSegment [constr] StartX=-16.8063 StartY=72.7682 StartZ=0 EndX=-16.8063 EndY=53.7182 EndZ=0
    g303: LineSegment [constr] StartX=-12.0438 StartY=72.7682 StartZ=0 EndX=-12.0438 EndY=53.7182 EndZ=0
    g304: LineSegment StartX=-23.8063 StartY=70.2432 StartZ=0 EndX=-9.80631 EndY=70.2432 EndZ=0
    g305: LineSegment StartX=-9.80631 StartY=70.2432 StartZ=0 EndX=-9.80631 EndY=56.2432 EndZ=0
    g306: LineSegment StartX=-9.80631 StartY=56.2432 StartZ=0 EndX=-23.8063 EndY=56.2432 EndZ=0
    g307: LineSegment StartX=-23.8063 StartY=56.2432 StartZ=0 EndX=-23.8063 EndY=70.2432 EndZ=0
    g308: LineSegment [constr] StartX=-7.28131 StartY=72.7682 StartZ=0 EndX=11.7687 EndY=72.7682 EndZ=0
    g309: LineSegment [constr] StartX=11.7687 StartY=72.7682 StartZ=0 EndX=11.7687 EndY=53.7182 EndZ=0
    g310: LineSegment [constr] StartX=11.7687 StartY=53.7182 StartZ=0 EndX=-7.28131 EndY=53.7182 EndZ=0
    g311: LineSegment [constr] StartX=-7.28131 StartY=53.7182 StartZ=0 EndX=-7.28131 EndY=72.7682 EndZ=0
    g312: LineSegment [constr] StartX=-2.51881 StartY=72.7682 StartZ=0 EndX=-2.51881 EndY=53.7182 EndZ=0
    g313: LineSegment [constr] StartX=2.24369 StartY=72.7682 StartZ=0 EndX=2.24369 EndY=53.7182 EndZ=0
    g314: LineSegment [constr] StartX=7.00619 StartY=72.7682 StartZ=0 EndX=7.00619 EndY=53.7182 EndZ=0
    g315: LineSegment StartX=-4.75631 StartY=70.2432 StartZ=0 EndX=9.24369 EndY=70.2432 EndZ=0
    g316: LineSegment StartX=9.24369 StartY=70.2432 StartZ=0 EndX=9.24369 EndY=56.2432 EndZ=0
    g317: LineSegment StartX=9.24369 StartY=56.2432 StartZ=0 EndX=-4.75631 EndY=56.2432 EndZ=0
    g318: LineSegment StartX=-4.75631 StartY=56.2432 StartZ=0 EndX=-4.75631 EndY=70.2432 EndZ=0
    g319: LineSegment [constr] StartX=11.7687 StartY=72.7682 StartZ=0 EndX=30.8187 EndY=72.7682 EndZ=0
    g320: LineSegment [constr] StartX=30.8187 StartY=72.7682 StartZ=0 EndX=30.8187 EndY=53.7182 EndZ=0
    g321: LineSegment [constr] StartX=30.8187 StartY=53.7182 StartZ=0 EndX=11.7687 EndY=53.7182 EndZ=0
    g322: LineSegment [constr] StartX=11.7687 StartY=53.7182 StartZ=0 EndX=11.7687 EndY=72.7682 EndZ=0
    g323: LineSegment [constr] StartX=16.5312 StartY=72.7682 StartZ=0 EndX=16.5312 EndY=53.7182 EndZ=0
    g324: LineSegment [constr] StartX=21.2937 StartY=72.7682 StartZ=0 EndX=21.2937 EndY=53.7182 EndZ=0
    g325: LineSegment [constr] StartX=26.0562 StartY=72.7682 StartZ=0 EndX=26.0562 EndY=53.7182 EndZ=0
    g326: LineSegment StartX=14.2937 StartY=70.2432 StartZ=0 EndX=28.2937 EndY=70.2432 EndZ=0
    g327: LineSegment StartX=28.2937 StartY=70.2432 StartZ=0 EndX=28.2937 EndY=56.2432 EndZ=0
    g328: LineSegment StartX=28.2937 StartY=56.2432 StartZ=0 EndX=14.2937 EndY=56.2432 EndZ=0
    g329: LineSegment StartX=14.2937 StartY=56.2432 StartZ=0 EndX=14.2937 EndY=70.2432 EndZ=0
    g330: LineSegment [constr] StartX=30.8187 StartY=72.7682 StartZ=0 EndX=49.8687 EndY=72.7682 EndZ=0
    g331: LineSegment [constr] StartX=49.8687 StartY=72.7682 StartZ=0 EndX=49.8687 EndY=53.7182 EndZ=0
    g332: LineSegment [constr] StartX=49.8687 StartY=53.7182 StartZ=0 EndX=30.8187 EndY=53.7182 EndZ=0
    g333: LineSegment [constr] StartX=30.8187 StartY=53.7182 StartZ=0 EndX=30.8187 EndY=72.7682 EndZ=0
    g334: LineSegment [constr] StartX=35.5812 StartY=72.7682 StartZ=0 EndX=35.5812 EndY=53.7182 EndZ=0
    g335: LineSegment [constr] StartX=40.3437 StartY=72.7682 StartZ=0 EndX=40.3437 EndY=53.7182 EndZ=0
    g336: LineSegment [constr] StartX=45.1062 StartY=72.7682 StartZ=0 EndX=45.1062 EndY=53.7182 EndZ=0
    g337: LineSegment StartX=33.3437 StartY=70.2432 StartZ=0 EndX=47.3437 EndY=70.2432 EndZ=0
    g338: LineSegment StartX=47.3437 StartY=70.2432 StartZ=0 EndX=47.3437 EndY=56.2432 EndZ=0
    g339: LineSegment StartX=47.3437 StartY=56.2432 StartZ=0 EndX=33.3437 EndY=56.2432 EndZ=0
    g340: LineSegment StartX=33.3437 StartY=56.2432 StartZ=0 EndX=33.3437 EndY=70.2432 EndZ=0
    g341: LineSegment [constr] StartX=49.8687 StartY=72.7682 StartZ=0 EndX=68.9187 EndY=72.7682 EndZ=0
    g342: LineSegment [constr] StartX=68.9187 StartY=72.7682 StartZ=0 EndX=68.9187 EndY=53.7182 EndZ=0
    g343: LineSegment [constr] StartX=68.9187 StartY=53.7182 StartZ=0 EndX=49.8687 EndY=53.7182 EndZ=0
    g344: LineSegment [constr] StartX=49.8687 StartY=53.7182 StartZ=0 EndX=49.8687 EndY=72.7682 EndZ=0
    g345: LineSegment [constr] StartX=54.6312 StartY=72.7682 StartZ=0 EndX=54.6312 EndY=53.7182 EndZ=0
    g346: LineSegment [constr] StartX=59.3937 StartY=72.7682 StartZ=0 EndX=59.3937 EndY=53.7182 EndZ=0
    g347: LineSegment [constr] StartX=64.1562 StartY=72.7682 StartZ=0 EndX=64.1562 EndY=53.7182 EndZ=0
    g348: LineSegment StartX=52.3937 StartY=70.2432 StartZ=0 EndX=66.3937 EndY=70.2432 EndZ=0
    g349: LineSegment StartX=66.3937 StartY=70.2432 StartZ=0 EndX=66.3937 EndY=56.2432 EndZ=0
    g350: LineSegment StartX=66.3937 StartY=56.2432 StartZ=0 EndX=52.3937 EndY=56.2432 EndZ=0
    g351: LineSegment StartX=52.3937 StartY=56.2432 StartZ=0 EndX=52.3937 EndY=70.2432 EndZ=0
    g352: LineSegment [constr] StartX=68.9187 StartY=72.7682 StartZ=0 EndX=87.9687 EndY=72.7682 EndZ=0
    g353: LineSegment [constr] StartX=87.9687 StartY=72.7682 StartZ=0 EndX=87.9687 EndY=53.7182 EndZ=0
    g354: LineSegment [constr] StartX=87.9687 StartY=53.7182 StartZ=0 EndX=68.9187 EndY=53.7182 EndZ=0
    g355: LineSegment [constr] StartX=68.9187 StartY=53.7182 StartZ=0 EndX=68.9187 EndY=72.7682 EndZ=0
    g356: LineSegment [constr] StartX=73.6812 StartY=72.7682 StartZ=0 EndX=73.6812 EndY=53.7182 EndZ=0
    g357: LineSegment [constr] StartX=78.4437 StartY=72.7682 StartZ=0 EndX=78.4437 EndY=53.7182 EndZ=0
    g358: LineSegment [constr] StartX=83.2062 StartY=72.7682 StartZ=0 EndX=83.2062 EndY=53.7182 EndZ=0
    g359: LineSegment StartX=71.4437 StartY=70.2432 StartZ=0 EndX=85.4437 EndY=70.2432 EndZ=0
    g360: LineSegment StartX=85.4437 StartY=70.2432 StartZ=0 EndX=85.4437 EndY=56.2432 EndZ=0
    g361: LineSegment StartX=85.4437 StartY=56.2432 StartZ=0 EndX=71.4437 EndY=56.2432 EndZ=0
    g362: LineSegment StartX=71.4437 StartY=56.2432 StartZ=0 EndX=71.4437 EndY=70.2432 EndZ=0
    g363: LineSegment [constr] StartX=87.9687 StartY=72.7682 StartZ=0 EndX=107.019 EndY=72.7682 EndZ=0
    g364: LineSegment [constr] StartX=107.019 StartY=72.7682 StartZ=0 EndX=107.019 EndY=53.7182 EndZ=0
    g365: LineSegment [constr] StartX=107.019 StartY=53.7182 StartZ=0 EndX=87.9687 EndY=53.7182 EndZ=0
    g366: LineSegment [constr] StartX=87.9687 StartY=53.7182 StartZ=0 EndX=87.9687 EndY=72.7682 EndZ=0
    g367: LineSegment [constr] StartX=92.7312 StartY=72.7682 StartZ=0 EndX=92.7312 EndY=53.7182 EndZ=0
    g368: LineSegment [constr] StartX=97.4937 StartY=72.7682 StartZ=0 EndX=97.4937 EndY=53.7182 EndZ=0
    g369: LineSegment [constr] StartX=102.256 StartY=72.7682 StartZ=0 EndX=102.256 EndY=53.7182 EndZ=0
    g370: LineSegment StartX=90.4937 StartY=70.2432 StartZ=0 EndX=104.494 EndY=70.2432 EndZ=0
    g371: LineSegment StartX=104.494 StartY=70.2432 StartZ=0 EndX=104.494 EndY=56.2432 EndZ=0
    g372: LineSegment StartX=104.494 StartY=56.2432 StartZ=0 EndX=90.4937 EndY=56.2432 EndZ=0
    g373: LineSegment StartX=90.4937 StartY=56.2432 StartZ=0 EndX=90.4937 EndY=70.2432 EndZ=0
    g374: LineSegment [constr] StartX=107.019 StartY=72.7682 StartZ=0 EndX=126.069 EndY=72.7682 EndZ=0
    g375: LineSegment [constr] StartX=126.069 StartY=72.7682 StartZ=0 EndX=126.069 EndY=53.7182 EndZ=0
    g376: LineSegment [constr] StartX=126.069 StartY=53.7182 StartZ=0 EndX=107.019 EndY=53.7182 EndZ=0
    g377: LineSegment [constr] StartX=107.019 StartY=53.7182 StartZ=0 EndX=107.019 EndY=72.7682 EndZ=0
    g378: LineSegment [constr] StartX=111.781 StartY=72.7682 StartZ=0 EndX=111.781 EndY=53.7182 EndZ=0
    g379: LineSegment [constr] StartX=116.544 StartY=72.7682 StartZ=0 EndX=116.544 EndY=53.7182 EndZ=0
    g380: LineSegment [constr] StartX=121.306 StartY=72.7682 StartZ=0 EndX=121.306 EndY=53.7182 EndZ=0
    g381: LineSegment StartX=109.544 StartY=70.2432 StartZ=0 EndX=123.544 EndY=70.2432 EndZ=0
    g382: LineSegment StartX=123.544 StartY=70.2432 StartZ=0 EndX=123.544 EndY=56.2432 EndZ=0
    g383: LineSegment StartX=123.544 StartY=56.2432 StartZ=0 EndX=109.544 EndY=56.2432 EndZ=0
    g384: LineSegment StartX=109.544 StartY=56.2432 StartZ=0 EndX=109.544 EndY=70.2432 EndZ=0
    g385: LineSegment [constr] StartX=126.069 StartY=72.7682 StartZ=0 EndX=145.119 EndY=72.7682 EndZ=0
    g386: LineSegment [constr] StartX=145.119 StartY=72.7682 StartZ=0 EndX=145.119 EndY=53.7182 EndZ=0
    g387: LineSegment [constr] StartX=145.119 StartY=53.7182 StartZ=0 EndX=126.069 EndY=53.7182 EndZ=0
    g388: LineSegment [constr] StartX=126.069 StartY=53.7182 StartZ=0 EndX=126.069 EndY=72.7682 EndZ=0
    g389: LineSegment [constr] StartX=130.831 StartY=72.7682 StartZ=0 EndX=130.831 EndY=53.7182 EndZ=0
    g390: LineSegment [constr] StartX=135.594 StartY=72.7682 StartZ=0 EndX=135.594 EndY=53.7182 EndZ=0
    g391: LineSegment [constr] StartX=140.356 StartY=72.7682 StartZ=0 EndX=140.356 EndY=53.7182 EndZ=0
    g392: LineSegment StartX=128.594 StartY=70.2432 StartZ=0 EndX=142.594 EndY=70.2432 EndZ=0
    g393: LineSegment StartX=142.594 StartY=70.2432 StartZ=0 EndX=142.594 EndY=56.2432 EndZ=0
    g394: LineSegment StartX=142.594 StartY=56.2432 StartZ=0 EndX=128.594 EndY=56.2432 EndZ=0
    g395: LineSegment StartX=128.594 StartY=56.2432 StartZ=0 EndX=128.594 EndY=70.2432 EndZ=0
    g396: LineSegment [constr] StartX=145.119 StartY=72.7682 StartZ=0 EndX=164.169 EndY=72.7682 EndZ=0
    g397: LineSegment [constr] StartX=164.169 StartY=72.7682 StartZ=0 EndX=164.169 EndY=53.7182 EndZ=0
    g398: LineSegment [constr] StartX=164.169 StartY=53.7182 StartZ=0 EndX=145.119 EndY=53.7182 EndZ=0
    g399: LineSegment [constr] StartX=145.119 StartY=53.7182 StartZ=0 EndX=145.119 EndY=72.7682 EndZ=0
    ... +604 more geometry lines
  constraints (2836):
    c: Coincident(g0,g1)
    c: Coincident(g1,g2)
    c: Coincident(g2,g3)
    c: Coincident(g3,g0)
    c: Horizontal(g0)
    c: Horizontal(g2)
    c: Vertical(g1)
    c: Vertical(g3)
    c: PointOnObject(g4,g2)
    c: PointOnObject(g5,g2)
    c: PointOnObject(g6,g2)
    c: Vertical(g6)
    c: Vertical(g4)
    c: Vertical(g5)
    c: Symmetric(g0,g0,g5)
    c: Symmetric(g0,g5,g4)
    c: Symmetric(g5,g0,g6)
    c: DistanceX(g0,g0) = 19.05
    c: DistanceY(g3,g3) = 19.05
    c: Coincident(g7,g8)
    c: Coincident(g8,g9)
    c: Coincident(g9,g10)
    c: Coincident(g10,g7)
    c: Horizontal(g7)
    c: Horizontal(g9)
    c: Vertical(g8)
    c: Vertical(g10)
    c: DistanceX(g7,g7) = 14
    c: DistanceY(g10,g10) = 14
    c: DistanceY(g7,g0) = 2.525
    c: DistanceX(g0,g7) = 2.525
    c: Coincident(g11,g12)
    c: Coincident(g12,g13)
    c: Coincident(g13,g14)
    c: Coincident(g14,g11)
    c: Horizontal(g11)
    c: Horizontal(g13)
    c: Vertical(g12)
    c: Vertical(g14)
    c: PointOnObject(g15,g13)
    c: PointOnObject(g16,g13)
    c: PointOnObject(g17,g13)
    c: Vertical(g17)
    c: Vertical(g15)
    c: Vertical(g16)
    c: Symmetric(g11,g11,g16)
    c: Symmetric(g11,g16,g15)
    c: Symmetric(g16,g11,g17)
    c: DistanceX(g11,g11) = 19.05
    c: DistanceY(g14,g14) = 19.05
    c: Coincident(g18,g11)
    c: Coincident(g19,g18)
    c: Vertical(g19)
    c: Coincident(g20,g19)
    c: Coincident(g20,g12)
    c: Horizontal(g20)
    c: PointOnObject(g21,g13)
    c: Vertical(g21)
    c: Symmetric(g16,g17,g21)
    c: Symmetric(g17,g18,g11)
    c: Coincident(g22,g23)
    c: Coincident(g23,g24)
    c: Coincident(g24,g25)
    c: Coincident(g25,g22)
    c: Horizontal(g22)
    c: Horizontal(g24)
    c: Vertical(g23)
    c: Vertical(g25)
    c: DistanceY(g25,g25) = 14
    c: DistanceX(g22,g22) = 14
    c: Symmetric(g22,g22,g26)
    c: PointOnObject(g26,g21)
    c: DistanceY(g26,g21) = 2.525
    c: Coincident(g27,g28)
    c: Coincident(g28,g29)
    c: Coincident(g29,g30)
    c: Coincident(g30,g27)
    c: Horizontal(g27)
    c: Horizontal(g29)
    c: Vertical(g28)
    c: Vertical(g30)
    c: PointOnObject(g31,g29)
    c: PointOnObject(g32,g29)
    c: PointOnObject(g33,g29)
    c: Vertical(g33)
    c: Vertical(g31)
    c: Vertical(g32)
    c: Symmetric(g27,g27,g32)
    c: Symmetric(g27,g32,g31)
    c: Symmetric(g32,g27,g33)
    c: DistanceX(g27,g27) = 19.05
    c: DistanceY(g30,g30) = 19.05
    c: Coincident(g34,g27)
    c: Coincident(g35,g34)
    c: Vertical(g35)
    c: Coincident(g36,g35)
    c: Coincident(g36,g28)
    c: Horizontal(g36)
    c: Symmetric(g33,g34,g27)
    c: Coincident(g37,g34)
    c: Vertical(g38)
    c: Coincident(g39,g38)
    c: Coincident(g39,g35)
    c: Horizontal(g39)
    c: Coincident(g38,g37)
    c: Symmetric(g27,g37,g34)
    c: Coincident(g40,g41)
    c: Coincident(g41,g42)
    c: Coincident(g42,g43)
    c: Coincident(g43,g40)
    c: Horizontal(g40)
    c: Horizontal(g42)
    c: Vertical(g41)
    c: Vertical(g43)
    c: DistanceX(g40,g40) = 14
    c: DistanceY(g43,g43) = 14
    c: PointOnObject(g44,g33)
    c: Symmetric(g40,g40,g44)
    c: DistanceY(g44,g33) = 2.525
    c: Coincident(g45,g46)
    c: Coincident(g46,g47)
    c: Coincident(g47,g48)
    c: Coincident(g48,g45)
    c: Horizontal(g45)
    c: Horizontal(g47)
    c: Vertical(g46)
    c: Vertical(g48)
    c: PointOnObject(g49,g47)
    c: PointOnObject(g50,g47)
    c: PointOnObject(g51,g47)
    c: Vertical(g51)
    c: Vertical(g49)
    c: Vertical(g50)
    c: Symmetric(g45,g45,g50)
    c: Symmetric(g45,g50,g49)
    c: Symmetric(g50,g45,g51)
    c: DistanceX(g45,g45) = 19.05
    c: DistanceY(g48,g48) = 19.05
    c: Coincident(g52,g45)
    c: Coincident(g53,g52)
    c: Vertical(g53)
    c: Coincident(g54,g53)
    c: Coincident(g54,g46)
    c: Horizontal(g54)
    c: Symmetric(g51,g52,g45)
    c: Coincident(g55,g52)
    c: Vertical(g56)
    c: Coincident(g57,g56)
    c: Coincident(g57,g53)
    c: Horizontal(g57)
    c: Coincident(g56,g55)
    c: Symmetric(g45,g55,g52)
    c: Coincident(g58,g55)
    c: Vertical(g59)
    c: Coincident(g60,g59)
    c: Coincident(g60,g56)
    c: Coincident(g58,g59)
    c: Horizontal(g60)
    c: Symmetric(g52,g58,g55)
    c: Vertical(g61)
    c: Symmetric(g51,g45,g61)
    c: Coincident(g62,g63)
    c: Coincident(g63,g64)
    c: Coincident(g64,g65)
    c: Coincident(g65,g62)
    c: Horizontal(g62)
    c: Horizontal(g64)
    c: Vertical(g63)
    c: Vertical(g65)
    c: DistanceX(g62,g62) = 14
    c: DistanceY(g65,g65) = 14
    c: Symmetric(g62,g62,g66)
    c: PointOnObject(g66,g61)
    c: DistanceY(g66,g61) = 2.525
    c: Coincident(g67,g68)
    c: Coincident(g68,g69)
    c: Coincident(g69,g70)
    c: Coincident(g70,g67)
    c: Horizontal(g67)
    c: Horizontal(g69)
    c: Vertical(g68)
    c: Vertical(g70)
    c: PointOnObject(g71,g69)
    c: PointOnObject(g72,g69)
    c: PointOnObject(g73,g69)
    c: Vertical(g73)
    c: Vertical(g71)
    c: Vertical(g72)
    c: Symmetric(g67,g67,g72)
    c: Symmetric(g67,g72,g71)
    c: Symmetric(g72,g67,g73)
    c: DistanceX(g67,g67) = 19.05
    c: DistanceY(g70,g70) = 19.05
    c: Coincident(g74,g67)
    c: Coincident(g75,g74)
    c: Vertical(g75)
    c: Coincident(g76,g75)
    c: Coincident(g76,g68)
    c: Horizontal(g76)
    c: Symmetric(g73,g74,g67)
    c: Coincident(g77,g74)
    c: Vertical(g78)
    c: Coincident(g79,g78)
    c: Coincident(g79,g75)
    c: Horizontal(g79)
    c: Coincident(g78,g77)
    c: Symmetric(g67,g77,g74)
    c: Coincident(g80,g77)
    c: Vertical(g81)
    c: Coincident(g82,g81)
    c: Coincident(g82,g78)
    c: Coincident(g80,g81)
    c: Horizontal(g82)
    c: Symmetric(g74,g80,g77)
    c: PointOnObject(g61,g47)
    c: Coincident(g83,g80)
    c: Coincident(g84,g83)
    c: Vertical(g84)
    c: Coincident(g85,g84)
    c: Coincident(g85,g81)
    c: Horizontal(g85)
    c: Symmetric(g77,g83,g80)
    c: Coincident(g86,g87)
    c: Coincident(g87,g88)
    c: Coincident(g88,g89)
    c: Coincident(g89,g86)
    c: Horizontal(g86)
    c: Horizontal(g88)
    c: Vertical(g87)
    c: Vertical(g89)
    c: DistanceY(g89,g89) = 14
    c: DistanceX(g86,g86) = 14
    c: Symmetric(g86,g86,g90)
    c: PointOnObject(g90,g68)
    c: DistanceY(g90,g67) = 2.525
    c: Coincident(g91,g92)
    c: Coincident(g92,g93)
    c: Coincident(g93,g94)
    c: Coincident(g94,g91)
    c: Horizontal(g91)
    c: Horizontal(g93)
    c: Vertical(g92)
    c: Vertical(g94)
    c: PointOnObject(g95,g93)
    c: PointOnObject(g96,g93)
    c: PointOnObject(g97,g93)
    c: Vertical(g97)
    c: Vertical(g95)
    c: Vertical(g96)
    c: Symmetric(g91,g91,g96)
    c: Symmetric(g91,g96,g95)
    c: Symmetric(g96,g91,g97)
    c: DistanceX(g91,g91) = 19.05
    c: DistanceY(g94,g94) = 19.05
    c: Coincident(g98,g91)
    c: Coincident(g99,g98)
    c: Vertical(g99)
    c: Coincident(g100,g99)
    c: Coincident(g100,g92)
    c: Horizontal(g100)
    c: Symmetric(g97,g98,g91)
    c: Coincident(g101,g98)
    c: Vertical(g102)
    c: Coincident(g103,g102)
    c: Coincident(g103,g99)
    c: Horizontal(g103)
    c: Coincident(g102,g101)
    c: Symmetric(g91,g101,g98)
    c: Coincident(g104,g101)
    c: Vertical(g105)
    c: Coincident(g106,g105)
    c: Coincident(g106,g102)
    c: Coincident(g104,g105)
    c: Horizontal(g106)
    c: Symmetric(g98,g104,g101)
    c: Coincident(g107,g104)
    c: Coincident(g108,g107)
    c: Vertical(g108)
    c: Coincident(g109,g108)
    c: Coincident(g109,g105)
    c: Horizontal(g109)
    c: Symmetric(g101,g107,g104)
    c: Coincident(g110,g107)
    c: Coincident(g111,g110)
    c: Vertical(g111)
    c: Coincident(g112,g111)
    c: Coincident(g112,g108)
    c: Horizontal(g112)
    c: Symmetric(g104,g110,g107)
    c: Vertical(g113)
    c: PointOnObject(g113,g100)
    c: Symmetric(g91,g98,g113)
    c: Coincident(g115,g116)
    c: Coincident(g116,g117)
    c: Coincident(g117,g118)
    c: Coincident(g118,g115)
    c: Horizontal(g115)
    c: Horizontal(g117)
    c: Vertical(g116)
    c: Vertical(g118)
    c: DistanceX(g115,g115) = 14
    c: DistanceY(g118,g118) = 14
    c: DistanceY(g114,g113) = 2.525
    c: Symmetric(g115,g115,g114)
    c: PointOnObject(g114,g113)
    c: Coincident(g119,g120)
    c: Coincident(g120,g121)
    c: Coincident(g121,g122)
    c: Coincident(g122,g119)
    c: Horizontal(g119)
    c: Horizontal(g121)
    c: Vertical(g120)
    c: Vertical(g122)
    c: PointOnObject(g123,g121)
    c: PointOnObject(g124,g121)
    c: PointOnObject(g125,g121)
    c: Vertical(g125)
    c: Vertical(g123)
    c: Vertical(g124)
    c: Symmetric(g119,g119,g124)
    c: Symmetric(g119,g124,g123)
    c: Symmetric(g124,g119,g125)
    c: DistanceX(g119,g119) = 19.05
    c: DistanceY(g122,g122) = 19.05
    c: Coincident(g126,g127)
    c: Coincident(g127,g128)
    c: Coincident(g128,g129)
    c: Coincident(g129,g126)
    c: Horizontal(g126)
    c: Horizontal(g128)
    c: Vertical(g127)
    c: Vertical(g129)
    c: DistanceX(g126,g126) = 14
    c: DistanceY(g129,g129) = 14
    c: DistanceY(g126,g119) = 2.525
    c: DistanceX(g119,g126) = 2.525
    c: Coincident(g130,g131)
    c: Coincident(g131,g132)
    c: Coincident(g132,g133)
    c: Coincident(g133,g130)
    c: Horizontal(g130)
    c: Horizontal(g132)
    c: Vertical(g131)
    c: Vertical(g133)
    c: PointOnObject(g134,g132)
    c: PointOnObject(g135,g132)
    c: PointOnObject(g136,g132)
    c: Vertical(g136)
    c: Vertical(g134)
    c: Vertical(g135)
    c: Symmetric(g130,g130,g135)
    c: Symmetric(g130,g135,g134)
    c: Symmetric(g135,g130,g136)
    c: DistanceX(g130,g130) = 19.05
    c: DistanceY(g133,g133) = 19.05
    c: Coincident(g137,g138)
    c: Coincident(g138,g139)
    c: Coincident(g139,g140)
    c: Coincident(g140,g137)
    c: Horizontal(g137)
    c: Horizontal(g139)
    c: Vertical(g138)
    c: Vertical(g140)
    c: DistanceX(g137,g137) = 14
    c: DistanceY(g140,g140) = 14
    c: DistanceY(g137,g130) = 2.525
    c: DistanceX(g130,g137) = 2.525
    c: DistanceX(g128,g139) = 28.575
    c: DistanceY(g139,g128) = 0
    c: Coincident(g141,g142)
    c: Coincident(g142,g143)
    c: Coincident(g143,g144)
    c: Coincident(g144,g141)
    c: Horizontal(g141)
    c: Horizontal(g143)
    c: Vertical(g142)
    c: Vertical(g144)
    c: PointOnObject(g145,g143)
    c: PointOnObject(g146,g143)
    c: PointOnObject(g147,g143)
    c: Vertical(g147)
    c: Vertical(g145)
    c: Vertical(g146)
    c: Symmetric(g141,g141,g146)
    c: Symmetric(g141,g146,g145)
    c: Symmetric(g146,g141,g147)
    c: DistanceX(g141,g141) = 19.05
    c: DistanceY(g144,g144) = 19.05
    c: Coincident(g148,g149)
    c: Coincident(g149,g150)
    c: Coincident(g150,g151)
    c: Coincident(g151,g148)
    c: Horizontal(g148)
    c: Horizontal(g150)
    c: Vertical(g149)
    c: Vertical(g151)
    c: DistanceX(g148,g148) = 14
    c: DistanceY(g151,g151) = 14
    c: DistanceY(g148,g141) = 2.525
    c: DistanceX(g141,g148) = 2.525
    c: Coincident(g143,g131)
    c: Coincident(g152,g153)
    c: Coincident(g153,g154)
    c: Coincident(g154,g155)
    c: Coincident(g155,g152)
    c: Horizontal(g152)
    c: Horizontal(g154)
    c: Vertical(g153)
    c: Vertical(g155)
    c: PointOnObject(g156,g154)
    c: PointOnObject(g157,g154)
    c: PointOnObject(g158,g154)
    c: Vertical(g158)
    c: Vertical(g156)
    c: Vertical(g157)
    c: Symmetric(g152,g152,g157)
    c: Symmetric(g152,g157,g156)
    c: Symmetric(g157,g152,g158)
    c: DistanceX(g152,g152) = 19.05
    c: DistanceY(g155,g155) = 19.05
    c: Coincident(g159,g160)
    c: Coincident(g160,g161)
    c: Coincident(g161,g162)
    c: Coincident(g162,g159)
    c: Horizontal(g159)
    c: Horizontal(g161)
    c: Vertical(g160)
    c: Vertical(g162)
    c: DistanceX(g159,g159) = 14
    c: DistanceY(g162,g162) = 14
    c: DistanceY(g159,g152) = 2.525
    c: DistanceX(g152,g159) = 2.525
    c: Coincident(g163,g164)
    c: Coincident(g164,g165)
    c: Coincident(g165,g166)
    c: Coincident(g166,g163)
    c: Horizontal(g163)
    c: Horizontal(g165)
    c: Vertical(g164)
    c: Vertical(g166)
    c: PointOnObject(g167,g165)
    c: PointOnObject(g168,g165)
    c: PointOnObject(g169,g165)
    c: Vertical(g169)
    c: Vertical(g167)
    c: Vertical(g168)
    c: Symmetric(g163,g163,g168)
    c: Symmetric(g163,g168,g167)
    c: Symmetric(g168,g163,g169)
    c: DistanceX(g163,g163) = 19.05
    c: DistanceY(g166,g166) = 19.05
    c: Coincident(g170,g171)
    c: Coincident(g171,g172)
    c: Coincident(g172,g173)
    c: Coincident(g173,g170)
    c: Horizontal(g170)
    c: Horizontal(g172)
    c: Vertical(g171)
    c: Vertical(g173)
    c: DistanceX(g170,g170) = 14
    c: DistanceY(g173,g173) = 14
    c: DistanceY(g170,g163) = 2.525
    c: DistanceX(g163,g170) = 2.525
    c: Coincident(g165,g153)
    c: Coincident(g154,g142)
    c: Coincident(g174,g175)
    c: Coincident(g175,g176)
    c: Coincident(g176,g177)
    c: Coincident(g177,g174)
    c: Horizontal(g174)
    c: Horizontal(g176)
    c: Vertical(g175)
    c: Vertical(g177)
    c: PointOnObject(g178,g176)
    c: PointOnObject(g179,g176)
    c: PointOnObject(g180,g176)
    c: Vertical(g180)
    c: Vertical(g178)
    c: Vertical(g179)
    c: Symmetric(g174,g174,g179)
    c: Symmetric(g174,g179,g178)
    c: Symmetric(g179,g174,g180)
    c: DistanceX(g174,g174) = 19.05
    c: DistanceY(g177,g177) = 19.05
    c: Coincident(g181,g182)
    c: Coincident(g182,g183)
    c: Coincident(g183,g184)
    c: Coincident(g184,g181)
    c: Horizontal(g181)
    c: Horizontal(g183)
    c: Vertical(g182)
    c: Vertical(g184)
    c: DistanceX(g181,g181) = 14
    c: DistanceY(g184,g184) = 14
    c: DistanceY(g181,g174) = 2.525
    c: DistanceX(g174,g181) = 2.525
    c: Coincident(g185,g186)
    c: Coincident(g186,g187)
    c: Coincident(g187,g188)
    c: Coincident(g188,g185)
    c: Horizontal(g185)
    c: Horizontal(g187)
    c: Vertical(g186)
    c: Vertical(g188)
    c: PointOnObject(g189,g187)
    c: PointOnObject(g190,g187)
    c: PointOnObject(g191,g187)
    c: Vertical(g191)
    c: Vertical(g189)
    c: Vertical(g190)
    c: Symmetric(g185,g185,g190)
    c: Symmetric(g185,g190,g189)
    c: Symmetric(g190,g185,g191)
    c: DistanceX(g185,g185) = 19.05
    c: DistanceY(g188,g188) = 19.05
    c: Coincident(g192,g193)
    c: Coincident(g193,g194)
    c: Coincident(g194,g195)
    c: Coincident(g195,g192)
    c: Horizontal(g192)
    c: Horizontal(g194)
    c: Vertical(g193)
    c: Vertical(g195)
    c: DistanceX(g192,g192) = 14
    c: DistanceY(g195,g195) = 14
    c: DistanceY(g192,g185) = 2.525
    c: DistanceX(g185,g192) = 2.525
    c: Coincident(g187,g175)
    c: Coincident(g196,g197)
    c: Coincident(g197,g198)
    c: Coincident(g198,g199)
    c: Coincident(g199,g196)
    c: Horizontal(g196)
    c: Horizontal(g198)
    c: Vertical(g197)
    c: Vertical(g199)
    c: PointOnObject(g200,g198)
    c: PointOnObject(g201,g198)
    c: PointOnObject(g202,g198)
    c: Vertical(g202)
    c: Vertical(g200)
    c: Vertical(g201)
    c: Symmetric(g196,g196,g201)
    c: Symmetric(g196,g201,g200)
    c: Symmetric(g201,g196,g202)
    c: DistanceX(g196,g196) = 19.05
    c: DistanceY(g199,g199) = 19.05
    c: Coincident(g203,g204)
    c: Coincident(g204,g205)
    c: Coincident(g205,g206)
    c: Coincident(g206,g203)
    c: Horizontal(g203)
    c: Horizontal(g205)
    c: Vertical(g204)
    c: Vertical(g206)
    c: DistanceX(g203,g203) = 14
    c: DistanceY(g206,g206) = 14
    c: DistanceY(g203,g196) = 2.525
    c: DistanceX(g196,g203) = 2.525
    c: Coincident(g207,g208)
    c: Coincident(g208,g209)
    c: Coincident(g209,g210)
    c: Coincident(g210,g207)
    c: Horizontal(g207)
    c: Horizontal(g209)
    c: Vertical(g208)
    c: Vertical(g210)
    c: PointOnObject(g211,g209)
    c: PointOnObject(g212,g209)
    c: PointOnObject(g213,g209)
    c: Vertical(g213)
    c: Vertical(g211)
    c: Vertical(g212)
    c: Symmetric(g207,g207,g212)
    c: Symmetric(g207,g212,g211)
    c: Symmetric(g212,g207,g213)
    c: DistanceX(g207,g207) = 19.05
    c: DistanceY(g210,g210) = 19.05
    c: Coincident(g214,g215)
    c: Coincident(g215,g216)
    c: Coincident(g216,g217)
    c: Coincident(g217,g214)
    c: Horizontal(g214)
    c: Horizontal(g216)
    c: Vertical(g215)
    c: Vertical(g217)
    c: DistanceX(g214,g214) = 14
    c: DistanceY(g217,g217) = 14
    c: DistanceY(g214,g207) = 2.525
    c: DistanceX(g207,g214) = 2.525
    c: Coincident(g209,g197)
    c: Coincident(g198,g186)
    c: DistanceY(g172,g183) = 0
    c: DistanceX(g164,g175) = 33.3375
    c: Coincident(g218,g219)
    c: Coincident(g219,g220)
    c: Coincident(g220,g221)
    c: Coincident(g221,g218)
    c: Horizontal(g218)
    c: Horizontal(g220)
    c: Vertical(g219)
    c: Vertical(g221)
    c: PointOnObject(g222,g220)
    c: PointOnObject(g223,g220)
    c: PointOnObject(g224,g220)
    c: Vertical(g224)
    c: Vertical(g222)
    c: Vertical(g223)
    c: Symmetric(g218,g218,g223)
    c: Symmetric(g218,g223,g222)
    c: Symmetric(g223,g218,g224)
    c: DistanceX(g218,g218) = 19.05
    c: DistanceY(g221,g221) = 19.05
    c: Coincident(g225,g226)
    c: Coincident(g226,g227)
    c: Coincident(g227,g228)
    c: Coincident(g228,g225)
    c: Horizontal(g225)
    c: Horizontal(g227)
    c: Vertical(g226)
    c: Vertical(g228)
    c: DistanceX(g225,g225) = 14
    c: DistanceY(g228,g228) = 14
    c: DistanceY(g225,g218) = 2.525
    c: DistanceX(g218,g225) = 2.525
    c: Coincident(g229,g230)
    c: Coincident(g230,g231)
    c: Coincident(g231,g232)
    c: Coincident(g232,g229)
    c: Horizontal(g229)
    c: Horizontal(g231)
    c: Vertical(g230)
    c: Vertical(g232)
    c: PointOnObject(g233,g231)
    c: PointOnObject(g234,g231)
    c: PointOnObject(g235,g231)
    c: Vertical(g235)
    c: Vertical(g233)
    c: Vertical(g234)
    c: Symmetric(g229,g229,g234)
    c: Symmetric(g229,g234,g233)
    c: Symmetric(g234,g229,g235)
    c: DistanceX(g229,g229) = 19.05
    c: DistanceY(g232,g232) = 19.05
    c: Coincident(g236,g237)
    c: Coincident(g237,g238)
    c: Coincident(g238,g239)
    c: Coincident(g239,g236)
    c: Horizontal(g236)
    c: Horizontal(g238)
    c: Vertical(g237)
    c: Vertical(g239)
    c: DistanceX(g236,g236) = 14
    c: DistanceY(g239,g239) = 14
    c: DistanceY(g236,g229) = 2.525
    c: DistanceX(g229,g236) = 2.525
    c: Coincident(g231,g219)
    c: Coincident(g240,g241)
    c: Coincident(g241,g242)
    c: Coincident(g242,g243)
    c: Coincident(g243,g240)
    c: Horizontal(g240)
    c: Horizontal(g242)
    c: Vertical(g241)
    c: Vertical(g243)
    c: PointOnObject(g244,g242)
    c: PointOnObject(g245,g242)
    c: PointOnObject(g246,g242)
    c: Vertical(g246)
    c: Vertical(g244)
    c: Vertical(g245)
    c: Symmetric(g240,g240,g245)
    c: Symmetric(g240,g245,g244)
    c: Symmetric(g245,g240,g246)
    c: DistanceX(g240,g240) = 19.05
    c: DistanceY(g243,g243) = 19.05
    c: Coincident(g247,g248)
    c: Coincident(g248,g249)
    c: Coincident(g249,g250)
    c: Coincident(g250,g247)
    c: Horizontal(g247)
    c: Horizontal(g249)
    c: Vertical(g248)
    c: Vertical(g250)
    c: DistanceX(g247,g247) = 14
    c: DistanceY(g250,g250) = 14
    c: DistanceY(g247,g240) = 2.525
    c: DistanceX(g240,g247) = 2.525
    c: Coincident(g251,g252)
    c: Coincident(g252,g253)
    c: Coincident(g253,g254)
    c: Coincident(g254,g251)
    c: Horizontal(g251)
    c: Horizontal(g253)
    c: Vertical(g252)
    c: Vertical(g254)
    c: PointOnObject(g255,g253)
    c: PointOnObject(g256,g253)
    c: PointOnObject(g257,g253)
    c: Vertical(g257)
    c: Vertical(g255)
    c: Vertical(g256)
    c: Symmetric(g251,g251,g256)
    c: Symmetric(g251,g256,g255)
    c: Symmetric(g256,g251,g257)
    c: DistanceX(g251,g251) = 19.05
    c: DistanceY(g254,g254) = 19.05
    c: Coincident(g258,g259)
    c: Coincident(g259,g260)
    c: Coincident(g260,g261)
    c: Coincident(g261,g258)
    c: Horizontal(g258)
    c: Horizontal(g260)
    c: Vertical(g259)
    c: Vertical(g261)
    c: DistanceX(g258,g258) = 14
    c: DistanceY(g261,g261) = 14
    c: DistanceY(g258,g251) = 2.525
    c: DistanceX(g251,g258) = 2.525
    c: Coincident(g253,g241)
    c: Coincident(g242,g230)
    c: DistanceX(g197,g220) = 33.3375
    c: DistanceY(g197,g220) = 0
    c: Coincident(g262,g263)
    c: Coincident(g263,g264)
    c: Coincident(g264,g265)
    c: Coincident(g265,g262)
    c: Horizontal(g262)
    c: Horizontal(g264)
    c: Vertical(g263)
    c: Vertical(g265)
    c: PointOnObject(g266,g264)
    c: PointOnObject(g267,g264)
    c: PointOnObject(g268,g264)
    c: Vertical(g268)
    c: Vertical(g266)
    c: Vertical(g267)
    c: Symmetric(g262,g262,g267)
    c: Symmetric(g262,g267,g266)
    c: Symmetric(g267,g262,g268)
    c: DistanceX(g262,g262) = 19.05
    c: DistanceY(g265,g265) = 19.05
    c: Coincident(g269,g270)
    c: Coincident(g270,g271)
    c: Coincident(g271,g272)
    c: Coincident(g272,g269)
    c: Horizontal(g269)
    c: Horizontal(g271)
    c: Vertical(g270)
    c: Vertical(g272)
    c: DistanceX(g269,g269) = 14
    c: DistanceY(g272,g272) = 14
    c: DistanceY(g269,g262) = 2.525
    c: DistanceX(g262,g269) = 2.525
    c: PointOnObject(g273,g263)
    c: Horizontal(g273)
    c: Symmetric(g264,g262,g273)
    c: PointOnObject(g274,g267)
    c: PointOnObject(g274,g273)
    c: Distance(g274,g252) = 18.9509
    c: Distance(g274,g251) = 18.829
    c: Coincident(g275,g276)
    c: Coincident(g276,g277)
    c: Coincident(g277,g278)
    c: Coincident(g278,g275)
    c: Horizontal(g275)
    c: Horizontal(g277)
    c: Vertical(g276)
    c: Vertical(g278)
    c: PointOnObject(g279,g277)
    c: PointOnObject(g280,g277)
    c: PointOnObject(g281,g277)
    c: Vertical(g281)
    c: Vertical(g279)
    c: Vertical(g280)
    c: Symmetric(g275,g275,g280)
    c: Symmetric(g275,g280,g279)
    c: Symmetric(g280,g275,g281)
    c: DistanceX(g275,g275) = 19.05
    c: DistanceY(g278,g278) = 19.05
    c: Coincident(g282,g283)
    c: Coincident(g283,g284)
    c: Coincident(g284,g285)
    c: Coincident(g285,g282)
    c: Horizontal(g282)
    c: Horizontal(g284)
    c: Vertical(g283)
    c: Vertical(g285)
    c: DistanceX(g282,g282) = 14
    c: DistanceY(g285,g285) = 14
    c: DistanceY(g282,g275) = 2.525
    c: DistanceX(g275,g282) = 2.525
    c: Coincident(g286,g287)
    c: Coincident(g287,g288)
    c: Coincident(g288,g289)
    c: Coincident(g289,g286)
    c: Horizontal(g286)
    c: Horizontal(g288)
    c: Vertical(g287)
    c: Vertical(g289)
    c: PointOnObject(g290,g288)
    c: PointOnObject(g291,g288)
    c: PointOnObject(g292,g288)
    c: Vertical(g292)
    c: Vertical(g290)
    c: Vertical(g291)
    c: Symmetric(g286,g286,g291)
    c: Symmetric(g286,g291,g290)
    c: Symmetric(g291,g286,g292)
    c: DistanceX(g286,g286) = 19.05
    c: DistanceY(g289,g289) = 19.05
    c: Coincident(g293,g294)
    c: Coincident(g294,g295)
    c: Coincident(g295,g296)
    c: Coincident(g296,g293)
    c: Horizontal(g293)
    c: Horizontal(g295)
    c: Vertical(g294)
    c: Vertical(g296)
    c: DistanceX(g293,g293) = 14
    c: DistanceY(g296,g296) = 14
    c: DistanceY(g293,g286) = 2.525
    c: DistanceX(g286,g293) = 2.525
    c: Coincident(g288,g276)
    c: Coincident(g297,g298)
    c: Coincident(g298,g299)
    c: Coincident(g299,g300)
    c: Coincident(g300,g297)
    c: Horizontal(g297)
    c: Horizontal(g299)
    c: Vertical(g298)
    c: Vertical(g300)
    c: PointOnObject(g301,g299)
    c: PointOnObject(g302,g299)
    c: PointOnObject(g303,g299)
    c: Vertical(g303)
    c: Vertical(g301)
    c: Vertical(g302)
    c: Symmetric(g297,g297,g302)
    c: Symmetric(g297,g302,g301)
    c: Symmetric(g302,g297,g303)
    c: DistanceX(g297,g297) = 19.05
    c: DistanceY(g300,g300) = 19.05
    c: Coincident(g304,g305)
    c: Coincident(g305,g306)
    c: Coincident(g306,g307)
    c: Coincident(g307,g304)
    c: Horizontal(g304)
    c: Horizontal(g306)
    c: Vertical(g305)
    c: Vertical(g307)
    c: DistanceX(g304,g304) = 14
    c: DistanceY(g307,g307) = 14
    c: DistanceY(g304,g297) = 2.525
    c: DistanceX(g297,g304) = 2.525
    c: Coincident(g308,g309)
    c: Coincident(g309,g310)
    c: Coincident(g310,g311)
    c: Coincident(g311,g308)
    c: Horizontal(g308)
    c: Horizontal(g310)
    c: Vertical(g309)
    c: Vertical(g311)
    c: PointOnObject(g312,g310)
    c: PointOnObject(g313,g310)
    c: PointOnObject(g314,g310)
    c: Vertical(g314)
    c: Vertical(g312)
    c: Vertical(g313)
    c: Symmetric(g308,g308,g313)
    c: Symmetric(g308,g313,g312)
    c: Symmetric(g313,g308,g314)
    c: DistanceX(g308,g308) = 19.05
    c: DistanceY(g311,g311) = 19.05
    c: Coincident(g315,g316)
    c: Coincident(g316,g317)
    c: Coincident(g317,g318)
    c: Coincident(g318,g315)
    c: Horizontal(g315)
    c: Horizontal(g317)
    c: Vertical(g316)
    c: Vertical(g318)
    c: DistanceX(g315,g315) = 14
    c: DistanceY(g318,g318) = 14
    c: DistanceY(g315,g308) = 2.525
    c: DistanceX(g308,g315) = 2.525
    c: Coincident(g310,g298)
    c: Coincident(g299,g287)
    c: DistanceX(g121,g275) = 0
    c: DistanceY(g277,g121) = 26.1925
    c: Coincident(g319,g320)
    c: Coincident(g320,g321)
    c: Coincident(g321,g322)
    c: Coincident(g322,g319)
    c: Horizontal(g319)
    c: Horizontal(g321)
    c: Vertical(g320)
    c: Vertical(g322)
    c: PointOnObject(g323,g321)
    c: PointOnObject(g324,g321)
    c: PointOnObject(g325,g321)
    c: Vertical(g325)
    c: Vertical(g323)
    c: Vertical(g324)
    c: Symmetric(g319,g319,g324)
    c: Symmetric(g319,g324,g323)
    c: Symmetric(g324,g319,g325)
    c: DistanceX(g319,g319) = 19.05
    c: DistanceY(g322,g322) = 19.05
    c: Coincident(g326,g327)
    c: Coincident(g327,g328)
    c: Coincident(g328,g329)
    c: Coincident(g329,g326)
    c: Horizontal(g326)
    c: Horizontal(g328)
    c: Vertical(g327)
    c: Vertical(g329)
    c: DistanceX(g326,g326) = 14
    c: DistanceY(g329,g329) = 14
    c: DistanceY(g326,g319) = 2.525
    c: DistanceX(g319,g326) = 2.525
    c: Coincident(g330,g331)
    c: Coincident(g331,g332)
    c: Coincident(g332,g333)
    c: Coincident(g333,g330)
    c: Horizontal(g330)
    c: Horizontal(g332)
    c: Vertical(g331)
    c: Vertical(g333)
    c: PointOnObject(g334,g332)
    c: PointOnObject(g335,g332)
    c: PointOnObject(g336,g332)
    c: Vertical(g336)
    c: Vertical(g334)
    c: Vertical(g335)
    c: Symmetric(g330,g330,g335)
    c: Symmetric(g330,g335,g334)
    c: Symmetric(g335,g330,g336)
    c: DistanceX(g330,g330) = 19.05
    c: DistanceY(g333,g333) = 19.05
    c: Coincident(g337,g338)
    c: Coincident(g338,g339)
    c: Coincident(g339,g340)
    c: Coincident(g340,g337)
    c: Horizontal(g337)
    c: Horizontal(g339)
    c: Vertical(g338)
    c: Vertical(g340)
    c: DistanceX(g337,g337) = 14
    c: DistanceY(g340,g340) = 14
    c: DistanceY(g337,g330) = 2.525
    c: DistanceX(g330,g337) = 2.525
    c: Coincident(g332,g320)
    c: Coincident(g341,g342)
    c: Coincident(g342,g343)
    c: Coincident(g343,g344)
    c: Coincident(g344,g341)
    c: Horizontal(g341)
    c: Horizontal(g343)
    c: Vertical(g342)
    c: Vertical(g344)
    c: PointOnObject(g345,g343)
    c: PointOnObject(g346,g343)
    c: PointOnObject(g347,g343)
    c: Vertical(g347)
    c: Vertical(g345)
    c: Vertical(g346)
    c: Symmetric(g341,g341,g346)
    c: Symmetric(g341,g346,g345)
    c: Symmetric(g346,g341,g347)
    c: DistanceX(g341,g341) = 19.05
    c: DistanceY(g344,g344) = 19.05
    c: Coincident(g348,g349)
    c: Coincident(g349,g350)
    c: Coincident(g350,g351)
    c: Coincident(g351,g348)
    c: Horizontal(g348)
    c: Horizontal(g350)
    c: Vertical(g349)
    c: Vertical(g351)
    c: DistanceX(g348,g348) = 14
    c: DistanceY(g351,g351) = 14
    c: DistanceY(g348,g341) = 2.525
    c: DistanceX(g341,g348) = 2.525
    c: Coincident(g352,g353)
    c: Coincident(g353,g354)
    c: Coincident(g354,g355)
    c: Coincident(g355,g352)
    c: Horizontal(g352)
    c: Horizontal(g354)
    c: Vertical(g353)
    c: Vertical(g355)
    c: PointOnObject(g356,g354)
    c: PointOnObject(g357,g354)
    c: PointOnObject(g358,g354)
    c: Vertical(g358)
    c: Vertical(g356)
    c: Vertical(g357)
    c: Symmetric(g352,g352,g357)
    c: Symmetric(g352,g357,g356)
    c: Symmetric(g357,g352,g358)
    c: DistanceX(g352,g352) = 19.05
    c: DistanceY(g355,g355) = 19.05
    c: Coincident(g359,g360)
    c: Coincident(g360,g361)
    c: Coincident(g361,g362)
    c: Coincident(g362,g359)
    c: Horizontal(g359)
    c: Horizontal(g361)
    c: Vertical(g360)
    c: Vertical(g362)
    c: DistanceX(g359,g359) = 14
    c: DistanceY(g362,g362) = 14
    c: DistanceY(g359,g352) = 2.525
    c: DistanceX(g352,g359) = 2.525
    c: Coincident(g354,g342)
    c: Coincident(g343,g331)
    c: Coincident(g321,g309)
    c: Coincident(g363,g364)
    c: Coincident(g364,g365)
    c: Coincident(g365,g366)
    c: Coincident(g366,g363)
    c: Horizontal(g363)
    c: Horizontal(g365)
    c: Vertical(g364)
    c: Vertical(g366)
    c: PointOnObject(g367,g365)
    c: PointOnObject(g368,g365)
    c: PointOnObject(g369,g365)
    c: Vertical(g369)
    c: Vertical(g367)
    c: Vertical(g368)
    c: Symmetric(g363,g363,g368)
    c: Symmetric(g363,g368,g367)
    c: Symmetric(g368,g363,g369)
    c: DistanceX(g363,g363) = 19.05
    c: DistanceY(g366,g366) = 19.05
    c: Coincident(g370,g371)
    c: Coincident(g371,g372)
    c: Coincident(g372,g373)
    c: Coincident(g373,g370)
    c: Horizontal(g370)
    c: Horizontal(g372)
    c: Vertical(g371)
    c: Vertical(g373)
    c: DistanceX(g370,g370) = 14
    c: DistanceY(g373,g373) = 14
    c: DistanceY(g370,g363) = 2.525
    c: DistanceX(g363,g370) = 2.525
    c: Coincident(g374,g375)
    c: Coincident(g375,g376)
    c: Coincident(g376,g377)
    c: Coincident(g377,g374)
    c: Horizontal(g374)
    c: Horizontal(g376)
    c: Vertical(g375)
    c: Vertical(g377)
    c: PointOnObject(g378,g376)
    c: PointOnObject(g379,g376)
    c: PointOnObject(g380,g376)
    c: Vertical(g380)
    c: Vertical(g378)
    c: Vertical(g379)
    c: Symmetric(g374,g374,g379)
    c: Symmetric(g374,g379,g378)
    c: Symmetric(g379,g374,g380)
    c: DistanceX(g374,g374) = 19.05
    c: DistanceY(g377,g377) = 19.05
    c: Coincident(g381,g382)
    c: Coincident(g382,g383)
    c: Coincident(g383,g384)
    c: Coincident(g384,g381)
    c: Horizontal(g381)
    c: Horizontal(g383)
    c: Vertical(g382)
    c: Vertical(g384)
    c: DistanceX(g381,g381) = 14
    c: DistanceY(g384,g384) = 14
    c: DistanceY(g381,g374) = 2.525
    c: DistanceX(g374,g381) = 2.525
    c: Coincident(g376,g364)
    c: Coincident(g385,g386)
    c: Coincident(g386,g387)
    c: Coincident(g387,g388)
    c: Coincident(g388,g385)
    c: Horizontal(g385)
    c: Horizontal(g387)
    c: Vertical(g386)
    c: Vertical(g388)
    c: PointOnObject(g389,g387)
    c: PointOnObject(g390,g387)
    c: PointOnObject(g391,g387)
    c: Vertical(g391)
    c: Vertical(g389)
    c: Vertical(g390)
    c: Symmetric(g385,g385,g390)
    c: Symmetric(g385,g390,g389)
    c: Symmetric(g390,g385,g391)
    c: DistanceX(g385,g385) = 19.05
    c: DistanceY(g388,g388) = 19.05
    c: Coincident(g392,g393)
    c: Coincident(g393,g394)
    c: Coincident(g394,g395)
    c: Coincident(g395,g392)
    c: Horizontal(g392)
    c: Horizontal(g394)
    c: Vertical(g393)
    c: Vertical(g395)
    c: DistanceX(g392,g392) = 14
    c: DistanceY(g395,g395) = 14
    c: DistanceY(g392,g385) = 2.525
    c: DistanceX(g385,g392) = 2.525
    c: Coincident(g396,g397)
    c: Coincident(g397,g398)
    c: Coincident(g398,g399)
    c: Coincident(g399,g396)
    c: Horizontal(g396)
    c: Horizontal(g398)
    c: Vertical(g397)
    c: Vertical(g399)
    c: PointOnObject(g400,g398)
    c: PointOnObject(g401,g398)
    c: PointOnObject(g402,g398)
    c: Vertical(g402)
    c: Vertical(g400)
    c: Vertical(g401)
    c: Symmetric(g396,g396,g401)
    c: Symmetric(g396,g401,g400)
    c: Symmetric(g401,g396,g402)
    c: DistanceX(g396,g396) = 19.05
    c: DistanceY(g399,g399) = 19.05
    c: Coincident(g403,g404)
    c: Coincident(g404,g405)
    c: Coincident(g405,g406)
    c: Coincident(g406,g403)
    c: Horizontal(g403)
    c: Horizontal(g405)
    c: Vertical(g404)
    c: Vertical(g406)
    c: DistanceX(g403,g403) = 14
    c: DistanceY(g406,g406) = 14
    c: DistanceY(g403,g396) = 2.525
    c: DistanceX(g396,g403) = 2.525
    c: Coincident(g398,g386)
    c: Coincident(g387,g375)
    c: Coincident(g365,g353)
    c: Coincident(g407,g408)
    c: Coincident(g408,g409)
    c: Coincident(g409,g410)
    c: Coincident(g410,g407)
    c: Horizontal(g407)
    c: Horizontal(g409)
    c: Vertical(g408)
    c: Vertical(g410)
    c: PointOnObject(g411,g409)
    c: PointOnObject(g412,g409)
    c: PointOnObject(g413,g409)
    c: Vertical(g413)
    c: Vertical(g411)
    c: Vertical(g412)
    c: Symmetric(g407,g407,g412)
    c: Symmetric(g407,g412,g411)
    c: Symmetric(g412,g407,g413)
    c: DistanceX(g407,g407) = 19.05
    c: DistanceY(g410,g410) = 19.05
    c: Coincident(g414,g415)
    c: Coincident(g415,g416)
    c: Coincident(g416,g417)
    c: Coincident(g417,g414)
    c: Horizontal(g414)
    c: Horizontal(g416)
    c: Vertical(g415)
    c: Vertical(g417)
    c: DistanceX(g414,g414) = 14
    c: DistanceY(g417,g417) = 14
    c: DistanceY(g414,g407) = 2.525
    c: DistanceX(g407,g414) = 2.525
    c: Coincident(g409,g397)
    c: Horizontal(g418)
    c: DistanceX(g418,g418) = 19.05
    c: Coincident(g418,g277)
    c: Coincident(g419,g420)
    c: Coincident(g420,g421)
    c: Coincident(g421,g422)
    c: Coincident(g422,g419)
    c: Horizontal(g419)
    c: Horizontal(g421)
    c: Vertical(g420)
    c: Vertical(g422)
    c: PointOnObject(g423,g421)
    c: PointOnObject(g424,g421)
    c: PointOnObject(g425,g421)
    c: Vertical(g425)
    c: Vertical(g423)
    c: Vertical(g424)
    c: Symmetric(g419,g419,g424)
    c: Symmetric(g419,g424,g423)
    c: Symmetric(g424,g419,g425)
    c: DistanceX(g419,g419) = 19.05
    c: DistanceY(g422,g422) = 19.05
    c: Coincident(g426,g427)
    c: Coincident(g427,g428)
    c: Coincident(g428,g429)
    c: Coincident(g429,g426)
    c: Horizontal(g426)
    c: Horizontal(g428)
    c: Vertical(g427)
    c: Vertical(g429)
    c: DistanceX(g426,g426) = 14
    c: DistanceY(g429,g429) = 14
    c: DistanceY(g426,g419) = 2.525
    c: DistanceX(g419,g426) = 2.525
    c: Coincident(g430,g431)
    c: Coincident(g431,g432)
    c: Coincident(g432,g433)
    c: Coincident(g433,g430)
    c: Horizontal(g430)
    c: Horizontal(g432)
    c: Vertical(g431)
    c: Vertical(g433)
    c: PointOnObject(g434,g432)
    c: PointOnObject(g435,g432)
    c: PointOnObject(g436,g432)
    c: Vertical(g436)
    c: Vertical(g434)
    c: Vertical(g435)
    c: Symmetric(g430,g430,g435)
    c: Symmetric(g430,g435,g434)
    c: Symmetric(g435,g430,g436)
    c: DistanceX(g430,g430) = 19.05
    c: DistanceY(g433,g433) = 19.05
    c: Coincident(g437,g438)
    c: Coincident(g438,g439)
    c: Coincident(g439,g440)
    c: Coincident(g440,g437)
    c: Horizontal(g437)
    c: Horizontal(g439)
    c: Vertical(g438)
    c: Vertical(g440)
    c: DistanceX(g437,g437) = 14
    c: DistanceY(g440,g440) = 14
    c: DistanceY(g437,g430) = 2.525
    c: DistanceX(g430,g437) = 2.525
    c: Coincident(g432,g420)
    c: Coincident(g441,g442)
    c: Coincident(g442,g443)
    c: Coincident(g443,g444)
    c: Coincident(g444,g441)
    c: Horizontal(g441)
    c: Horizontal(g443)
    c: Vertical(g442)
    c: Vertical(g444)
    c: PointOnObject(g445,g443)
    c: PointOnObject(g446,g443)
    c: PointOnObject(g447,g443)
    c: Vertical(g447)
    c: Vertical(g445)
    c: Vertical(g446)
    c: Symmetric(g441,g441,g446)
    c: Symmetric(g441,g446,g445)
    c: Symmetric(g446,g441,g447)
    c: DistanceX(g441,g441) = 19.05
    c: DistanceY(g444,g444) = 19.05
    c: Coincident(g448,g449)
    c: Coincident(g449,g450)
    c: Coincident(g450,g451)
    c: Coincident(g451,g448)
    c: Horizontal(g448)
    c: Horizontal(g450)
    c: Vertical(g449)
    c: Vertical(g451)
    c: DistanceX(g448,g448) = 14
    c: DistanceY(g451,g451) = 14
    c: DistanceY(g448,g441) = 2.525
    c: DistanceX(g441,g448) = 2.525
    c: Coincident(g452,g453)
    c: Coincident(g453,g454)
    c: Coincident(g454,g455)
    c: Coincident(g455,g452)
    c: Horizontal(g452)
    c: Horizontal(g454)
    c: Vertical(g453)
    c: Vertical(g455)
    c: PointOnObject(g456,g454)
    c: PointOnObject(g457,g454)
    c: PointOnObject(g458,g454)
    c: Vertical(g458)
    c: Vertical(g456)
    c: Vertical(g457)
    c: Symmetric(g452,g452,g457)
    c: Symmetric(g452,g457,g456)
    c: Symmetric(g457,g452,g458)
    c: DistanceX(g452,g452) = 19.05
    c: DistanceY(g455,g455) = 19.05
    c: Coincident(g459,g460)
    c: Coincident(g460,g461)
    c: Coincident(g461,g462)
    c: Coincident(g462,g459)
    c: Horizontal(g459)
    c: Horizontal(g461)
    c: Vertical(g460)
    c: Vertical(g462)
    c: DistanceX(g459,g459) = 14
    c: DistanceY(g462,g462) = 14
    c: DistanceY(g459,g452) = 2.525
    c: DistanceX(g452,g459) = 2.525
    c: Coincident(g454,g442)
    c: Coincident(g443,g431)
    c: Coincident(g463,g464)
    c: Coincident(g464,g465)
    c: Coincident(g465,g466)
    c: Coincident(g466,g463)
    c: Horizontal(g463)
    c: Horizontal(g465)
    c: Vertical(g464)
    c: Vertical(g466)
    c: PointOnObject(g467,g465)
    c: PointOnObject(g468,g465)
    c: PointOnObject(g469,g465)
    c: Vertical(g469)
    c: Vertical(g467)
    c: Vertical(g468)
    c: Symmetric(g463,g463,g468)
    c: Symmetric(g463,g468,g467)
    c: Symmetric(g468,g463,g469)
    c: DistanceX(g463,g463) = 19.05
    c: DistanceY(g466,g466) = 19.05
    c: Coincident(g470,g471)
    c: Coincident(g471,g472)
    c: Coincident(g472,g473)
    c: Coincident(g473,g470)
    c: Horizontal(g470)
    c: Horizontal(g472)
    c: Vertical(g471)
    c: Vertical(g473)
    c: DistanceX(g470,g470) = 14
    c: DistanceY(g473,g473) = 14
    c: DistanceY(g470,g463) = 2.525
    c: DistanceX(g463,g470) = 2.525
    c: Coincident(g474,g475)
    c: Coincident(g475,g476)
    c: Coincident(g476,g477)
    c: Coincident(g477,g474)
    c: Horizontal(g474)
    c: Horizontal(g476)
    c: Vertical(g475)
    c: Vertical(g477)
    c: PointOnObject(g478,g476)
    c: PointOnObject(g479,g476)
    c: PointOnObject(g480,g476)
    c: Vertical(g480)
    c: Vertical(g478)
    c: Vertical(g479)
    c: Symmetric(g474,g474,g479)
    c: Symmetric(g474,g479,g478)
    c: Symmetric(g479,g474,g480)
    c: DistanceX(g474,g474) = 19.05
    c: DistanceY(g477,g477) = 19.05
    c: Coincident(g481,g482)
    c: Coincident(g482,g483)
    c: Coincident(g483,g484)
    c: Coincident(g484,g481)
    c: Horizontal(g481)
    c: Horizontal(g483)
    c: Vertical(g482)
    c: Vertical(g484)
    c: DistanceX(g481,g481) = 14
    c: DistanceY(g484,g484) = 14
    c: DistanceY(g481,g474) = 2.525
    c: DistanceX(g474,g481) = 2.525
    c: Coincident(g476,g464)
    c: Coincident(g485,g486)
    c: Coincident(g486,g487)
    c: Coincident(g487,g488)
    c: Coincident(g488,g485)
    c: Horizontal(g485)
    c: Horizontal(g487)
    c: Vertical(g486)
    c: Vertical(g488)
    c: PointOnObject(g489,g487)
    c: PointOnObject(g490,g487)
    c: PointOnObject(g491,g487)
    c: Vertical(g491)
    c: Vertical(g489)
    c: Vertical(g490)
    c: Symmetric(g485,g485,g490)
    c: Symmetric(g485,g490,g489)
    c: Symmetric(g490,g485,g491)
    c: DistanceX(g485,g485) = 19.05
    c: DistanceY(g488,g488) = 19.05
    c: Coincident(g492,g493)
    c: Coincident(g493,g494)
    c: Coincident(g494,g495)
    c: Coincident(g495,g492)
    c: Horizontal(g492)
    c: Horizontal(g494)
    c: Vertical(g493)
    c: Vertical(g495)
    c: DistanceX(g492,g492) = 14
    c: DistanceY(g495,g495) = 14
    c: DistanceY(g492,g485) = 2.525
    c: DistanceX(g485,g492) = 2.525
    c: Coincident(g496,g497)
    c: Coincident(g497,g498)
    c: Coincident(g498,g499)
    c: Coincident(g499,g496)
    c: Horizontal(g496)
    c: Horizontal(g498)
    c: Vertical(g497)
    c: Vertical(g499)
    c: PointOnObject(g500,g498)
    c: PointOnObject(g501,g498)
    c: PointOnObject(g502,g498)
    c: Vertical(g502)
    c: Vertical(g500)
    c: Vertical(g501)
    c: Symmetric(g496,g496,g501)
    c: Symmetric(g496,g501,g500)
    c: Symmetric(g501,g496,g502)
    c: DistanceX(g496,g496) = 19.05
    c: DistanceY(g499,g499) = 19.05
    c: Coincident(g503,g504)
    c: Coincident(g504,g505)
    c: Coincident(g505,g506)
    c: Coincident(g506,g503)
    c: Horizontal(g503)
    c: Horizontal(g505)
    c: Vertical(g504)
    c: Vertical(g506)
    c: DistanceX(g503,g503) = 14
    c: DistanceY(g506,g506) = 14
    c: DistanceY(g503,g496) = 2.525
    c: DistanceX(g496,g503) = 2.525
    c: Coincident(g498,g486)
    c: Coincident(g487,g475)
    c: Coincident(g463,g452)
    c: Coincident(g507,g508)
    c: Coincident(g508,g509)
    c: Coincident(g509,g510)
    c: Coincident(g510,g507)
    c: Horizontal(g507)
    c: Horizontal(g509)
    c: Vertical(g508)
    c: Vertical(g510)
    c: PointOnObject(g511,g509)
    c: PointOnObject(g512,g509)
    c: PointOnObject(g513,g509)
    c: Vertical(g513)
    c: Vertical(g511)
    c: Vertical(g512)
    c: Symmetric(g507,g507,g512)
    c: Symmetric(g507,g512,g511)
    c: Symmetric(g512,g507,g513)
    c: DistanceX(g507,g507) = 19.05
    c: DistanceY(g510,g510) = 19.05
    c: Coincident(g514,g515)
    c: Coincident(g515,g516)
    c: Coincident(g516,g517)
    c: Coincident(g517,g514)
    c: Horizontal(g514)
    c: Horizontal(g516)
    c: Vertical(g515)
    c: Vertical(g517)
    c: DistanceX(g514,g514) = 14
    c: DistanceY(g517,g517) = 14
    c: DistanceY(g514,g507) = 2.525
    c: DistanceX(g507,g514) = 2.525
    c: Coincident(g518,g519)
    c: Coincident(g519,g520)
    c: Coincident(g520,g521)
    c: Coincident(g521,g518)
    c: Horizontal(g518)
    c: Horizontal(g520)
    c: Vertical(g519)
    c: Vertical(g521)
    c: PointOnObject(g522,g520)
    c: PointOnObject(g523,g520)
    c: PointOnObject(g524,g520)
    c: Vertical(g524)
    c: Vertical(g522)
    c: Vertical(g523)
    c: Symmetric(g518,g518,g523)
    c: Symmetric(g518,g523,g522)
    c: Symmetric(g523,g518,g524)
    c: DistanceX(g518,g518) = 19.05
    c: DistanceY(g521,g521) = 19.05
    c: Coincident(g525,g526)
    c: Coincident(g526,g527)
    c: Coincident(g527,g528)
    c: Coincident(g528,g525)
    c: Horizontal(g525)
    c: Horizontal(g527)
    c: Vertical(g526)
    c: Vertical(g528)
    c: DistanceX(g525,g525) = 14
    c: DistanceY(g528,g528) = 14
    c: DistanceY(g525,g518) = 2.525
    c: DistanceX(g518,g525) = 2.525
    c: Coincident(g520,g508)
    c: Coincident(g529,g530)
    c: Coincident(g530,g531)
    c: Coincident(g531,g532)
    c: Coincident(g532,g529)
    c: Horizontal(g529)
    c: Horizontal(g531)
    c: Vertical(g530)
    c: Vertical(g532)
    c: PointOnObject(g533,g531)
    c: PointOnObject(g534,g531)
    c: PointOnObject(g535,g531)
    c: Vertical(g535)
    c: Vertical(g533)
    c: Vertical(g534)
    c: Symmetric(g529,g529,g534)
    c: Symmetric(g529,g534,g533)
    c: Symmetric(g534,g529,g535)
    c: DistanceX(g529,g529) = 19.05
    c: DistanceY(g532,g532) = 19.05
    c: Coincident(g536,g537)
    c: Coincident(g537,g538)
    c: Coincident(g538,g539)
    c: Coincident(g539,g536)
    c: Horizontal(g536)
    c: Horizontal(g538)
    c: Vertical(g537)
    c: Vertical(g539)
    c: DistanceX(g536,g536) = 14
    c: DistanceY(g539,g539) = 14
    c: DistanceY(g536,g529) = 2.525
    c: DistanceX(g529,g536) = 2.525
    c: Coincident(g540,g541)
    c: Coincident(g541,g542)
    c: Coincident(g542,g543)
    c: Coincident(g543,g540)
    c: Horizontal(g540)
    c: Horizontal(g542)
    c: Vertical(g541)
    c: Vertical(g543)
    c: PointOnObject(g544,g542)
    c: PointOnObject(g545,g542)
    c: PointOnObject(g546,g542)
    c: Vertical(g546)
    c: Vertical(g544)
    c: Vertical(g545)
    c: Symmetric(g540,g540,g545)
    c: Symmetric(g540,g545,g544)
    c: Symmetric(g545,g540,g546)
    c: DistanceX(g540,g540) = 19.05
    c: DistanceY(g543,g543) = 19.05
    c: Coincident(g547,g548)
    c: Coincident(g548,g549)
    c: Coincident(g549,g550)
    c: Coincident(g550,g547)
    c: Horizontal(g547)
    c: Horizontal(g549)
    c: Vertical(g548)
    c: Vertical(g550)
    c: DistanceX(g547,g547) = 14
    c: DistanceY(g550,g550) = 14
    c: DistanceY(g547,g540) = 2.525
    c: DistanceX(g540,g547) = 2.525
    c: Coincident(g542,g530)
    c: Coincident(g531,g519)
    c: Coincident(g509,g497)
    c: Coincident(g419,g291)
    c: Coincident(g551,g552)
    c: Coincident(g552,g553)
    c: Coincident(g553,g554)
    c: Coincident(g554,g551)
    c: Horizontal(g551)
    c: Horizontal(g553)
    c: Vertical(g552)
    c: Vertical(g554)
    c: PointOnObject(g555,g553)
    c: PointOnObject(g556,g553)
    c: PointOnObject(g557,g553)
    c: Vertical(g557)
    c: Vertical(g555)
    c: Vertical(g556)
    c: Symmetric(g551,g551,g556)
    c: Symmetric(g551,g556,g555)
    c: Symmetric(g556,g551,g557)
    c: DistanceX(g551,g551) = 19.05
    c: DistanceY(g554,g554) = 19.05
    c: Coincident(g558,g559)
    c: Coincident(g559,g560)
    c: Coincident(g560,g561)
    c: Coincident(g561,g558)
    c: Horizontal(g558)
    c: Horizontal(g560)
    c: Vertical(g559)
    c: Vertical(g561)
    c: DistanceX(g558,g558) = 14
    c: DistanceY(g561,g561) = 14
    c: DistanceY(g558,g551) = 2.525
    c: DistanceX(g551,g558) = 2.525
    c: Coincident(g562,g563)
    c: Coincident(g563,g564)
    c: Coincident(g564,g565)
    c: Coincident(g565,g562)
    c: Horizontal(g562)
    c: Horizontal(g564)
    c: Vertical(g563)
    c: Vertical(g565)
    c: PointOnObject(g566,g564)
    c: PointOnObject(g567,g564)
    c: PointOnObject(g568,g564)
    c: Vertical(g568)
    c: Vertical(g566)
    c: Vertical(g567)
    c: Symmetric(g562,g562,g567)
    c: Symmetric(g562,g567,g566)
    c: Symmetric(g567,g562,g568)
    c: DistanceX(g562,g562) = 19.05
    c: DistanceY(g565,g565) = 19.05
    c: Coincident(g569,g570)
    c: Coincident(g570,g571)
    c: Coincident(g571,g572)
    c: Coincident(g572,g569)
    c: Horizontal(g569)
    c: Horizontal(g571)
    c: Vertical(g570)
    c: Vertical(g572)
    c: DistanceX(g569,g569) = 14
    c: DistanceY(g572,g572) = 14
    c: DistanceY(g569,g562) = 2.525
    c: DistanceX(g562,g569) = 2.525
    c: Coincident(g564,g552)
    c: Coincident(g573,g574)
    c: Coincident(g574,g575)
    c: Coincident(g575,g576)
    c: Coincident(g576,g573)
    c: Horizontal(g573)
    c: Horizontal(g575)
    c: Vertical(g574)
    c: Vertical(g576)
    c: PointOnObject(g577,g575)
    c: PointOnObject(g578,g575)
    c: PointOnObject(g579,g575)
    c: Vertical(g579)
    c: Vertical(g577)
    c: Vertical(g578)
    c: Symmetric(g573,g573,g578)
    c: Symmetric(g573,g578,g577)
    c: Symmetric(g578,g573,g579)
    c: DistanceX(g573,g573) = 19.05
    c: DistanceY(g576,g576) = 19.05
    c: Coincident(g580,g581)
    c: Coincident(g581,g582)
    c: Coincident(g582,g583)
    c: Coincident(g583,g580)
    c: Horizontal(g580)
    c: Horizontal(g582)
    c: Vertical(g581)
    c: Vertical(g583)
    c: DistanceX(g580,g580) = 14
    c: DistanceY(g583,g583) = 14
    c: DistanceY(g580,g573) = 2.525
    c: DistanceX(g573,g580) = 2.525
    c: Coincident(g584,g585)
    c: Coincident(g585,g586)
    c: Coincident(g586,g587)
    c: Coincident(g587,g584)
    c: Horizontal(g584)
    c: Horizontal(g586)
    c: Vertical(g585)
    c: Vertical(g587)
    c: PointOnObject(g588,g586)
    c: PointOnObject(g589,g586)
    c: PointOnObject(g590,g586)
    c: Vertical(g590)
    c: Vertical(g588)
    c: Vertical(g589)
    c: Symmetric(g584,g584,g589)
    c: Symmetric(g584,g589,g588)
    c: Symmetric(g589,g584,g590)
    c: DistanceX(g584,g584) = 19.05
    c: DistanceY(g587,g587) = 19.05
    c: Coincident(g591,g592)
    c: Coincident(g592,g593)
    c: Coincident(g593,g594)
    c: Coincident(g594,g591)
    c: Horizontal(g591)
    c: Horizontal(g593)
    c: Vertical(g592)
    c: Vertical(g594)
    c: DistanceX(g591,g591) = 14
    c: DistanceY(g594,g594) = 14
    c: DistanceY(g591,g584) = 2.525
    c: DistanceX(g584,g591) = 2.525
    c: Coincident(g586,g574)
    c: Coincident(g575,g563)
    c: Coincident(g595,g596)
    c: Coincident(g596,g597)
    c: Coincident(g597,g598)
    c: Coincident(g598,g595)
    c: Horizontal(g595)
    c: Horizontal(g597)
    c: Vertical(g596)
    c: Vertical(g598)
    c: PointOnObject(g599,g597)
    c: PointOnObject(g600,g597)
    c: PointOnObject(g601,g597)
    c: Vertical(g601)
    c: Vertical(g599)
    c: Vertical(g600)
    c: Symmetric(g595,g595,g600)
    c: Symmetric(g595,g600,g599)
    c: Symmetric(g600,g595,g601)
    c: DistanceX(g595,g595) = 19.05
    c: DistanceY(g598,g598) = 19.05
    c: Coincident(g602,g603)
    c: Coincident(g603,g604)
    c: Coincident(g604,g605)
    c: Coincident(g605,g602)
    c: Horizontal(g602)
    c: Horizontal(g604)
    c: Vertical(g603)
    c: Vertical(g605)
    c: DistanceX(g602,g602) = 14
    c: DistanceY(g605,g605) = 14
    c: DistanceY(g602,g595) = 2.525
    c: DistanceX(g595,g602) = 2.525
    c: Coincident(g606,g607)
    c: Coincident(g607,g608)
    c: Coincident(g608,g609)
    c: Coincident(g609,g606)
    c: Horizontal(g606)
    c: Horizontal(g608)
    c: Vertical(g607)
    c: Vertical(g609)
    c: PointOnObject(g610,g608)
    c: PointOnObject(g611,g608)
    c: PointOnObject(g612,g608)
    c: Vertical(g612)
    c: Vertical(g610)
    c: Vertical(g611)
    c: Symmetric(g606,g606,g611)
    c: Symmetric(g606,g611,g610)
    c: Symmetric(g611,g606,g612)
    c: DistanceX(g606,g606) = 19.05
    c: DistanceY(g609,g609) = 19.05
    c: Coincident(g613,g614)
    c: Coincident(g614,g615)
    c: Coincident(g615,g616)
    c: Coincident(g616,g613)
    c: Horizontal(g613)
    c: Horizontal(g615)
    c: Vertical(g614)
    c: Vertical(g616)
    c: DistanceX(g613,g613) = 14
    c: DistanceY(g616,g616) = 14
    c: DistanceY(g613,g606) = 2.525
    c: DistanceX(g606,g613) = 2.525
    c: Coincident(g608,g596)
    c: Coincident(g617,g618)
    c: Coincident(g618,g619)
    c: Coincident(g619,g620)
    c: Coincident(g620,g617)
    c: Horizontal(g617)
    c: Horizontal(g619)
    c: Vertical(g618)
    c: Vertical(g620)
    c: PointOnObject(g621,g619)
    c: PointOnObject(g622,g619)
    c: PointOnObject(g623,g619)
    c: Vertical(g623)
    c: Vertical(g621)
    c: Vertical(g622)
    c: Symmetric(g617,g617,g622)
    c: Symmetric(g617,g622,g621)
    c: Symmetric(g622,g617,g623)
    c: DistanceX(g617,g617) = 19.05
    c: DistanceY(g620,g620) = 19.05
    c: Coincident(g624,g625)
    c: Coincident(g625,g626)
    c: Coincident(g626,g627)
    c: Coincident(g627,g624)
    c: Horizontal(g624)
    c: Horizontal(g626)
    c: Vertical(g625)
    c: Vertical(g627)
    c: DistanceX(g624,g624) = 14
    c: DistanceY(g627,g627) = 14
    c: DistanceY(g624,g617) = 2.525
    c: DistanceX(g617,g624) = 2.525
    c: Coincident(g628,g629)
    c: Coincident(g629,g630)
    c: Coincident(g630,g631)
    c: Coincident(g631,g628)
    c: Horizontal(g628)
    c: Horizontal(g630)
    c: Vertical(g629)
    c: Vertical(g631)
    c: PointOnObject(g632,g630)
    c: PointOnObject(g633,g630)
    c: PointOnObject(g634,g630)
    c: Vertical(g634)
    c: Vertical(g632)
    c: Vertical(g633)
    c: Symmetric(g628,g628,g633)
    c: Symmetric(g628,g633,g632)
    c: Symmetric(g633,g628,g634)
    c: DistanceX(g628,g628) = 19.05
    c: DistanceY(g631,g631) = 19.05
    c: Coincident(g635,g636)
    c: Coincident(g636,g637)
    c: Coincident(g637,g638)
    c: Coincident(g638,g635)
    c: Horizontal(g635)
    c: Horizontal(g637)
    c: Vertical(g636)
    c: Vertical(g638)
    c: DistanceX(g635,g635) = 14
    c: DistanceY(g638,g638) = 14
    c: DistanceY(g635,g628) = 2.525
    c: DistanceX(g628,g635) = 2.525
    c: Coincident(g630,g618)
    c: Coincident(g619,g607)
    c: Coincident(g639,g640)
    c: Coincident(g640,g641)
    c: Coincident(g641,g642)
    c: Coincident(g642,g639)
    c: Horizontal(g639)
    c: Horizontal(g641)
    c: Vertical(g640)
    c: Vertical(g642)
    c: PointOnObject(g643,g641)
    c: PointOnObject(g644,g641)
    c: PointOnObject(g645,g641)
    c: Vertical(g645)
    c: Vertical(g643)
    c: Vertical(g644)
    c: Symmetric(g639,g639,g644)
    c: Symmetric(g639,g644,g643)
    c: Symmetric(g644,g639,g645)
    c: DistanceX(g639,g639) = 19.05
    c: DistanceY(g642,g642) = 19.05
    c: Coincident(g646,g647)
    c: Coincident(g647,g648)
    c: Coincident(g648,g649)
    c: Coincident(g649,g646)
    c: Horizontal(g646)
    c: Horizontal(g648)
    c: Vertical(g647)
    c: Vertical(g649)
    c: DistanceX(g646,g646) = 14
    c: DistanceY(g649,g649) = 14
    c: DistanceY(g646,g639) = 2.525
    c: DistanceX(g639,g646) = 2.525
    c: Coincident(g650,g651)
    c: Coincident(g651,g652)
    c: Coincident(g652,g653)
    c: Coincident(g653,g650)
    c: Horizontal(g650)
    c: Horizontal(g652)
    c: Vertical(g651)
    c: Vertical(g653)
    c: PointOnObject(g654,g652)
    c: PointOnObject(g655,g652)
    c: PointOnObject(g656,g652)
    c: Vertical(g656)
    c: Vertical(g654)
    c: Vertical(g655)
    c: Symmetric(g650,g650,g655)
    c: Symmetric(g650,g655,g654)
    c: Symmetric(g655,g650,g656)
    c: DistanceX(g650,g650) = 19.05
    c: DistanceY(g653,g653) = 19.05
    c: Coincident(g657,g658)
    c: Coincident(g658,g659)
    c: Coincident(g659,g660)
    c: Coincident(g660,g657)
    c: Horizontal(g657)
    c: Horizontal(g659)
    c: Vertical(g658)
    c: Vertical(g660)
    c: DistanceX(g657,g657) = 14
    c: DistanceY(g660,g660) = 14
    c: DistanceY(g657,g650) = 2.525
    c: DistanceX(g650,g657) = 2.525
    c: Coincident(g652,g640)
    c: Coincident(g661,g662)
    c: Coincident(g662,g663)
    c: Coincident(g663,g664)
    c: Coincident(g664,g661)
    c: Horizontal(g661)
    c: Horizontal(g663)
    c: Vertical(g662)
    c: Vertical(g664)
    c: PointOnObject(g665,g663)
    c: PointOnObject(g666,g663)
    c: PointOnObject(g667,g663)
    c: Vertical(g667)
    c: Vertical(g665)
    c: Vertical(g666)
    c: Symmetric(g661,g661,g666)
    c: Symmetric(g661,g666,g665)
    c: Symmetric(g666,g661,g667)
    c: DistanceX(g661,g661) = 19.05
    c: DistanceY(g664,g664) = 19.05
    c: Coincident(g668,g669)
    c: Coincident(g669,g670)
    c: Coincident(g670,g671)
    c: Coincident(g671,g668)
    c: Horizontal(g668)
    c: Horizontal(g670)
    c: Vertical(g669)
    c: Vertical(g671)
    c: DistanceX(g668,g668) = 14
    c: DistanceY(g671,g671) = 14
    c: DistanceY(g668,g661) = 2.525
    c: DistanceX(g661,g668) = 2.525
    c: Coincident(g663,g651)
    c: Coincident(g597,g585)
    c: Coincident(g629,g641)
    c: Coincident(g672,g673)
    c: Coincident(g673,g674)
    c: Coincident(g674,g675)
    c: Coincident(g675,g672)
    c: Horizontal(g672)
    c: Horizontal(g674)
    c: Vertical(g673)
    c: Vertical(g675)
    c: PointOnObject(g676,g674)
    c: PointOnObject(g677,g674)
    c: PointOnObject(g678,g674)
    c: Vertical(g678)
    c: Vertical(g676)
    c: Vertical(g677)
    c: Symmetric(g672,g672,g677)
    c: Symmetric(g672,g677,g676)
    c: Symmetric(g677,g672,g678)
    c: DistanceX(g672,g672) = 19.05
    c: DistanceY(g675,g675) = 19.05
    c: Coincident(g679,g680)
    c: Coincident(g680,g681)
    c: Coincident(g681,g682)
    c: Coincident(g682,g679)
    c: Horizontal(g679)
    c: Horizontal(g681)
    c: Vertical(g680)
    c: Vertical(g682)
    c: DistanceX(g679,g679) = 14
    c: DistanceY(g682,g682) = 14
    c: DistanceY(g679,g672) = 2.525
    c: DistanceX(g672,g679) = 2.525
    c: Coincident(g683,g684)
    c: Coincident(g684,g685)
    c: Coincident(g685,g686)
    c: Coincident(g686,g683)
    c: Horizontal(g683)
    c: Horizontal(g685)
    c: Vertical(g684)
    c: Vertical(g686)
    c: PointOnObject(g687,g685)
    c: PointOnObject(g688,g685)
    c: PointOnObject(g689,g685)
    c: Vertical(g689)
    c: Vertical(g687)
    c: Vertical(g688)
    c: Symmetric(g683,g683,g688)
    c: Symmetric(g683,g688,g687)
    c: Symmetric(g688,g683,g689)
    c: DistanceX(g683,g683) = 19.05
    c: DistanceY(g686,g686) = 19.05
    c: Coincident(g690,g691)
    c: Coincident(g691,g692)
    c: Coincident(g692,g693)
    c: Coincident(g693,g690)
    c: Horizontal(g690)
    c: Horizontal(g692)
    c: Vertical(g691)
    c: Vertical(g693)
    c: DistanceX(g690,g690) = 14
    c: DistanceY(g693,g693) = 14
    c: DistanceY(g690,g683) = 2.525
    c: DistanceX(g683,g690) = 2.525
    c: Coincident(g685,g673)
    c: Coincident(g694,g695)
    c: Coincident(g695,g696)
    c: Coincident(g696,g697)
    c: Coincident(g697,g694)
    c: Horizontal(g694)
    c: Horizontal(g696)
    c: Vertical(g695)
    c: Vertical(g697)
    c: PointOnObject(g698,g696)
    c: PointOnObject(g699,g696)
    c: PointOnObject(g700,g696)
    c: Vertical(g700)
    c: Vertical(g698)
    c: Vertical(g699)
    c: Symmetric(g694,g694,g699)
    c: Symmetric(g694,g699,g698)
    c: Symmetric(g699,g694,g700)
    c: DistanceX(g694,g694) = 19.05
    c: DistanceY(g697,g697) = 19.05
    c: Coincident(g701,g702)
    c: Coincident(g702,g703)
    c: Coincident(g703,g704)
    c: Coincident(g704,g701)
    c: Horizontal(g701)
    c: Horizontal(g703)
    c: Vertical(g702)
    c: Vertical(g704)
    c: DistanceX(g701,g701) = 14
    c: DistanceY(g704,g704) = 14
    c: DistanceY(g701,g694) = 2.525
    c: DistanceX(g694,g701) = 2.525
    c: Coincident(g705,g706)
    c: Coincident(g706,g707)
    c: Coincident(g707,g708)
    c: Coincident(g708,g705)
    c: Horizontal(g705)
    c: Horizontal(g707)
    c: Vertical(g706)
    c: Vertical(g708)
    c: PointOnObject(g709,g707)
    c: PointOnObject(g710,g707)
    c: PointOnObject(g711,g707)
    c: Vertical(g711)
    c: Vertical(g709)
    c: Vertical(g710)
    c: Symmetric(g705,g705,g710)
    c: Symmetric(g705,g710,g709)
    c: Symmetric(g710,g705,g711)
    c: DistanceX(g705,g705) = 19.05
    c: DistanceY(g708,g708) = 19.05
    c: Coincident(g712,g713)
    c: Coincident(g713,g714)
    c: Coincident(g714,g715)
    c: Coincident(g715,g712)
    c: Horizontal(g712)
    c: Horizontal(g714)
    c: Vertical(g713)
    c: Vertical(g715)
    c: DistanceX(g712,g712) = 14
    c: DistanceY(g715,g715) = 14
    c: DistanceY(g712,g705) = 2.525
    c: DistanceX(g705,g712) = 2.525
    c: Coincident(g707,g695)
    c: Coincident(g696,g684)
    c: Coincident(g716,g717)
    c: Coincident(g717,g718)
    c: Coincident(g718,g719)
    c: Coincident(g719,g716)
    c: Horizontal(g716)
    c: Horizontal(g718)
    c: Vertical(g717)
    c: Vertical(g719)
    c: PointOnObject(g720,g718)
    c: PointOnObject(g721,g718)
    c: PointOnObject(g722,g718)
    c: Vertical(g722)
    c: Vertical(g720)
    c: Vertical(g721)
    c: Symmetric(g716,g716,g721)
    c: Symmetric(g716,g721,g720)
    c: Symmetric(g721,g716,g722)
    c: DistanceX(g716,g716) = 19.05
    c: DistanceY(g719,g719) = 19.05
    c: Coincident(g723,g724)
    c: Coincident(g724,g725)
    c: Coincident(g725,g726)
    c: Coincident(g726,g723)
    c: Horizontal(g723)
    c: Horizontal(g725)
    c: Vertical(g724)
    c: Vertical(g726)
    c: DistanceX(g723,g723) = 14
    c: DistanceY(g726,g726) = 14
    c: DistanceY(g723,g716) = 2.525
    c: DistanceX(g716,g723) = 2.525
    c: Coincident(g727,g728)
    c: Coincident(g728,g729)
    c: Coincident(g729,g730)
    c: Coincident(g730,g727)
    c: Horizontal(g727)
    c: Horizontal(g729)
    c: Vertical(g728)
    c: Vertical(g730)
    c: PointOnObject(g731,g729)
    c: PointOnObject(g732,g729)
    c: PointOnObject(g733,g729)
    c: Vertical(g733)
    c: Vertical(g731)
    c: Vertical(g732)
    c: Symmetric(g727,g727,g732)
    c: Symmetric(g727,g732,g731)
    c: Symmetric(g732,g727,g733)
    c: DistanceX(g727,g727) = 19.05
    c: DistanceY(g730,g730) = 19.05
    c: Coincident(g734,g735)
    c: Coincident(g735,g736)
    c: Coincident(g736,g737)
    c: Coincident(g737,g734)
    c: Horizontal(g734)
    c: Horizontal(g736)
    c: Vertical(g735)
    c: Vertical(g737)
    c: DistanceX(g734,g734) = 14
    c: DistanceY(g737,g737) = 14
    c: DistanceY(g734,g727) = 2.525
    c: DistanceX(g727,g734) = 2.525
    c: Coincident(g729,g717)
    c: Coincident(g738,g739)
    c: Coincident(g739,g740)
    c: Coincident(g740,g741)
    c: Coincident(g741,g738)
    c: Horizontal(g738)
    c: Horizontal(g740)
    c: Vertical(g739)
    c: Vertical(g741)
    c: PointOnObject(g742,g740)
    c: PointOnObject(g743,g740)
    c: PointOnObject(g744,g740)
    c: Vertical(g744)
    c: Vertical(g742)
    c: Vertical(g743)
    c: Symmetric(g738,g738,g743)
    c: Symmetric(g738,g743,g742)
    c: Symmetric(g743,g738,g744)
    c: DistanceX(g738,g738) = 19.05
    c: DistanceY(g741,g741) = 19.05
    c: Coincident(g745,g746)
    c: Coincident(g746,g747)
    c: Coincident(g747,g748)
    c: Coincident(g748,g745)
    c: Horizontal(g745)
    c: Horizontal(g747)
    c: Vertical(g746)
    c: Vertical(g748)
    c: DistanceX(g745,g745) = 14
    c: DistanceY(g748,g748) = 14
    c: DistanceY(g745,g738) = 2.525
    c: DistanceX(g738,g745) = 2.525
    c: Coincident(g749,g750)
    c: Coincident(g750,g751)
    c: Coincident(g751,g752)
    c: Coincident(g752,g749)
    c: Horizontal(g749)
    c: Horizontal(g751)
    c: Vertical(g750)
    c: Vertical(g752)
    c: PointOnObject(g753,g751)
    c: PointOnObject(g754,g751)
    c: PointOnObject(g755,g751)
    c: Vertical(g755)
    c: Vertical(g753)
    c: Vertical(g754)
    c: Symmetric(g749,g749,g754)
    c: Symmetric(g749,g754,g753)
    c: Symmetric(g754,g749,g755)
    c: DistanceX(g749,g749) = 19.05
    c: DistanceY(g752,g752) = 19.05
    c: Coincident(g756,g757)
    c: Coincident(g757,g758)
    c: Coincident(g758,g759)
    c: Coincident(g759,g756)
    c: Horizontal(g756)
    c: Horizontal(g758)
    c: Vertical(g757)
    c: Vertical(g759)
    c: DistanceX(g756,g756) = 14
    c: DistanceY(g759,g759) = 14
    c: DistanceY(g756,g749) = 2.525
    c: DistanceX(g749,g756) = 2.525
    c: Coincident(g751,g739)
    c: Coincident(g740,g728)
    c: Coincident(g760,g761)
    c: Coincident(g761,g762)
    c: Coincident(g762,g763)
    c: Coincident(g763,g760)
    c: Horizontal(g760)
    c: Horizontal(g762)
    c: Vertical(g761)
    c: Vertical(g763)
    c: PointOnObject(g764,g762)
    c: PointOnObject(g765,g762)
    c: PointOnObject(g766,g762)
    c: Vertical(g766)
    c: Vertical(g764)
    c: Vertical(g765)
    c: Symmetric(g760,g760,g765)
    c: Symmetric(g760,g765,g764)
    c: Symmetric(g765,g760,g766)
    c: DistanceX(g760,g760) = 19.05
    c: DistanceY(g763,g763) = 19.05
    c: Coincident(g767,g768)
    c: Coincident(g768,g769)
    c: Coincident(g769,g770)
    c: Coincident(g770,g767)
    c: Horizontal(g767)
    c: Horizontal(g769)
    c: Vertical(g768)
    c: Vertical(g770)
    c: DistanceX(g767,g767) = 14
    c: DistanceY(g770,g770) = 14
    c: DistanceY(g767,g760) = 2.525
    c: DistanceX(g760,g767) = 2.525
    c: Coincident(g771,g772)
    c: Coincident(g772,g773)
    c: Coincident(g773,g774)
    c: Coincident(g774,g771)
    c: Horizontal(g771)
    c: Horizontal(g773)
    c: Vertical(g772)
    c: Vertical(g774)
    c: PointOnObject(g775,g773)
    c: PointOnObject(g776,g773)
    c: PointOnObject(g777,g773)
    c: Vertical(g777)
    c: Vertical(g775)
    c: Vertical(g776)
    c: Symmetric(g771,g771,g776)
    c: Symmetric(g771,g776,g775)
    c: Symmetric(g776,g771,g777)
    c: DistanceX(g771,g771) = 19.05
    c: DistanceY(g774,g774) = 19.05
    c: Coincident(g778,g779)
    c: Coincident(g779,g780)
    c: Coincident(g780,g781)
    c: Coincident(g781,g778)
    c: Horizontal(g778)
    c: Horizontal(g780)
    c: Vertical(g779)
    c: Vertical(g781)
    c: DistanceX(g778,g778) = 14
    c: DistanceY(g781,g781) = 14
    c: DistanceY(g778,g771) = 2.525
    c: DistanceX(g771,g778) = 2.525
    c: Coincident(g773,g761)
    c: Coincident(g718,g706)
    c: Coincident(g750,g762)
    c: Coincident(g672,g556)
    c: Coincident(g544,g661)
    c: Coincident(g782,g783)
    c: Coincident(g783,g784)
    c: Coincident(g784,g785)
    c: Coincident(g785,g782)
    c: Horizontal(g782)
    c: Horizontal(g784)
    c: Vertical(g783)
    c: Vertical(g785)
    c: PointOnObject(g786,g784)
    c: PointOnObject(g787,g784)
    c: PointOnObject(g788,g784)
    c: Vertical(g788)
    c: Vertical(g786)
    c: Vertical(g787)
    c: Symmetric(g782,g782,g787)
    c: Symmetric(g782,g787,g786)
    c: Symmetric(g787,g782,g788)
    c: DistanceX(g782,g782) = 19.05
    c: DistanceY(g785,g785) = 19.05
    c: Coincident(g789,g782)
    c: Coincident(g790,g789)
    c: Vertical(g790)
    c: Coincident(g791,g790)
    c: Coincident(g791,g783)
    c: Horizontal(g791)
    c: Symmetric(g788,g789,g782)
    c: Coincident(g792,g789)
    c: Vertical(g793)
    c: Coincident(g794,g793)
    c: Coincident(g794,g790)
    c: Horizontal(g794)
    c: Coincident(g793,g792)
    c: Symmetric(g782,g792,g789)
    c: Coincident(g795,g796)
    c: Coincident(g796,g797)
    c: Coincident(g797,g798)
    c: Coincident(g798,g795)
    c: Horizontal(g795)
    c: Horizontal(g797)
    c: Vertical(g796)
    c: Vertical(g798)
    c: DistanceX(g795,g795) = 14
    c: DistanceY(g798,g798) = 14
    c: PointOnObject(g799,g788)
    c: Symmetric(g795,g795,g799)
    c: DistanceY(g799,g788) = 2.525
    c: Coincident(g782,g277)
    c: Coincident(g800,g801)
    c: Coincident(g801,g802)
    c: Coincident(g802,g803)
    c: Coincident(g803,g800)
    c: Horizontal(g800)
    c: Horizontal(g802)
    c: Vertical(g801)
    c: Vertical(g803)
    c: PointOnObject(g804,g802)
    c: PointOnObject(g805,g802)
    c: PointOnObject(g806,g802)
    c: Vertical(g806)
    c: Vertical(g804)
    c: Vertical(g805)
    c: Symmetric(g800,g800,g805)
    c: Symmetric(g800,g805,g804)
    c: Symmetric(g805,g800,g806)
    c: DistanceX(g800,g800) = 19.05
    c: DistanceY(g803,g803) = 19.05
    c: Coincident(g807,g800)
    c: Coincident(g808,g807)
    c: Vertical(g808)
    c: Coincident(g809,g808)
    c: Coincident(g809,g801)
    c: Horizontal(g809)
    c: Symmetric(g806,g807,g800)
    c: Coincident(g810,g807)
    c: Vertical(g811)
    c: Coincident(g812,g811)
    c: Coincident(g812,g808)
    c: Horizontal(g812)
    c: Coincident(g811,g810)
    c: Symmetric(g800,g810,g807)
    c: Coincident(g813,g810)
    c: Vertical(g814)
    c: Coincident(g815,g814)
    c: Coincident(g815,g811)
    c: Coincident(g813,g814)
    c: Horizontal(g815)
    c: Symmetric(g807,g813,g810)
    c: Vertical(g816)
    c: Symmetric(g806,g800,g816)
    c: Coincident(g817,g818)
    c: Coincident(g818,g819)
    c: Coincident(g819,g820)
    c: Coincident(g820,g817)
    c: Horizontal(g817)
    c: Horizontal(g819)
    c: Vertical(g818)
    c: Vertical(g820)
    c: DistanceX(g817,g817) = 14
    c: DistanceY(g820,g820) = 14
    c: Symmetric(g817,g817,g821)
    c: PointOnObject(g821,g816)
    c: DistanceY(g821,g816) = 2.525
    c: PointOnObject(g816,g802)
    c: Coincident(g784,g800)
    c: Coincident(g822,g823)
    c: Coincident(g823,g824)
    c: Coincident(g824,g825)
    c: Coincident(g825,g822)
    c: Horizontal(g822)
    c: Horizontal(g824)
    c: Vertical(g823)
    c: Vertical(g825)
    c: PointOnObject(g826,g824)
    c: PointOnObject(g827,g824)
    c: PointOnObject(g828,g824)
    c: Vertical(g828)
    c: Vertical(g826)
    c: Vertical(g827)
    c: Symmetric(g822,g822,g827)
    c: Symmetric(g822,g827,g826)
    c: Symmetric(g827,g822,g828)
    c: DistanceX(g822,g822) = 19.05
    c: DistanceY(g825,g825) = 19.05
    c: Coincident(g829,g830)
    c: Coincident(g830,g831)
    c: Coincident(g831,g832)
    c: Coincident(g832,g829)
    c: Horizontal(g829)
    c: Horizontal(g831)
    c: Vertical(g830)
    c: Vertical(g832)
    c: DistanceX(g829,g829) = 14
    c: DistanceY(g832,g832) = 14
    c: DistanceY(g829,g822) = 2.525
    c: DistanceX(g822,g829) = 2.525
    c: Coincident(g833,g834)
    c: Coincident(g834,g835)
    c: Coincident(g835,g836)
    c: Coincident(g836,g833)
    c: Horizontal(g833)
    c: Horizontal(g835)
    c: Vertical(g834)
    c: Vertical(g836)
    c: PointOnObject(g837,g835)
    c: PointOnObject(g838,g835)
    c: PointOnObject(g839,g835)
    c: Vertical(g839)
    c: Vertical(g837)
    c: Vertical(g838)
    c: Symmetric(g833,g833,g838)
    c: Symmetric(g833,g838,g837)
    c: Symmetric(g838,g833,g839)
    c: DistanceX(g833,g833) = 19.05
    c: DistanceY(g836,g836) = 19.05
    c: Coincident(g840,g841)
    c: Coincident(g841,g842)
    c: Coincident(g842,g843)
    c: Coincident(g843,g840)
    c: Horizontal(g840)
    c: Horizontal(g842)
    c: Vertical(g841)
    c: Vertical(g843)
    c: DistanceX(g840,g840) = 14
    c: DistanceY(g843,g843) = 14
    c: DistanceY(g840,g833) = 2.525
    c: DistanceX(g833,g840) = 2.525
    c: Coincident(g844,g845)
    c: Coincident(g845,g846)
    c: Coincident(g846,g847)
    c: Coincident(g847,g844)
    c: Horizontal(g844)
    c: Horizontal(g846)
    c: Vertical(g845)
    c: Vertical(g847)
    c: PointOnObject(g848,g846)
    c: PointOnObject(g849,g846)
    c: PointOnObject(g850,g846)
    c: Vertical(g850)
    c: Vertical(g848)
    c: Vertical(g849)
    c: Symmetric(g844,g844,g849)
    c: Symmetric(g844,g849,g848)
    c: Symmetric(g849,g844,g850)
    c: DistanceX(g844,g844) = 19.05
    c: DistanceY(g847,g847) = 19.05
    c: Coincident(g851,g852)
    c: Coincident(g852,g853)
    c: Coincident(g853,g854)
    c: Coincident(g854,g851)
    c: Horizontal(g851)
    c: Horizontal(g853)
    c: Vertical(g852)
    c: Vertical(g854)
    c: DistanceX(g851,g851) = 14
    c: DistanceY(g854,g854) = 14
    c: DistanceY(g851,g844) = 2.525
    c: DistanceX(g844,g851) = 2.525
    c: Coincident(g846,g834)
    c: Coincident(g835,g823)
    c: Coincident(g855,g856)
    c: Coincident(g856,g857)
    c: Coincident(g857,g858)
    c: Coincident(g858,g855)
    c: Horizontal(g855)
    c: Horizontal(g857)
    c: Vertical(g856)
    c: Vertical(g858)
    c: PointOnObject(g859,g857)
    c: PointOnObject(g860,g857)
    c: PointOnObject(g861,g857)
    c: Vertical(g861)
    c: Vertical(g859)
    c: Vertical(g860)
    c: Symmetric(g855,g855,g860)
    c: Symmetric(g855,g860,g859)
    c: Symmetric(g860,g855,g861)
    c: DistanceX(g855,g855) = 19.05
    c: DistanceY(g858,g858) = 19.05
    c: Coincident(g862,g855)
    c: Coincident(g863,g862)
    c: Vertical(g863)
    c: Coincident(g864,g863)
    c: Coincident(g864,g856)
    c: Horizontal(g864)
    c: PointOnObject(g865,g857)
    c: Vertical(g865)
    c: Symmetric(g860,g861,g865)
    c: Symmetric(g861,g862,g855)
    c: Coincident(g866,g867)
    c: Coincident(g867,g868)
    c: Coincident(g868,g869)
    c: Coincident(g869,g866)
    c: Horizontal(g866)
    c: Horizontal(g868)
    c: Vertical(g867)
    c: Vertical(g869)
    c: DistanceY(g869,g869) = 14
    c: DistanceX(g866,g866) = 14
    c: Symmetric(g866,g866,g870)
    c: PointOnObject(g870,g865)
    c: DistanceY(g870,g865) = 2.525
    c: Coincident(g857,g845)
    c: Coincident(g684,g862)
    c: Coincident(g871,g872)
    c: Coincident(g872,g873)
    c: Coincident(g873,g874)
    c: Coincident(g874,g871)
    c: Horizontal(g871)
    c: Horizontal(g873)
    c: Vertical(g872)
    c: Vertical(g874)
    c: PointOnObject(g875,g873)
    c: PointOnObject(g876,g873)
    c: PointOnObject(g877,g873)
    c: Vertical(g877)
    c: Vertical(g875)
    c: Vertical(g876)
    c: Symmetric(g871,g871,g876)
    c: Symmetric(g871,g876,g875)
    c: Symmetric(g876,g871,g877)
    c: DistanceX(g871,g871) = 19.05
    c: DistanceY(g874,g874) = 19.05
    c: Coincident(g878,g871)
    c: Coincident(g879,g878)
    c: Vertical(g879)
    c: Coincident(g880,g879)
    c: Coincident(g880,g872)
    c: Horizontal(g880)
    c: PointOnObject(g881,g873)
    c: Vertical(g881)
    c: Symmetric(g876,g877,g881)
    c: Symmetric(g877,g878,g871)
    c: Coincident(g882,g883)
    c: Coincident(g883,g884)
    c: Coincident(g884,g885)
    c: Coincident(g885,g882)
    c: Horizontal(g882)
    c: Horizontal(g884)
    c: Vertical(g883)
    c: Vertical(g885)
    c: DistanceY(g885,g885) = 14
    c: DistanceX(g882,g882) = 14
    c: Symmetric(g882,g882,g886)
    c: PointOnObject(g886,g881)
    c: DistanceY(g886,g881) = 2.525
    c: Coincident(g887,g888)
    c: Coincident(g888,g889)
    c: Coincident(g889,g890)
    c: Coincident(g890,g887)
    c: Horizontal(g887)
    c: Horizontal(g889)
    c: Vertical(g888)
    c: Vertical(g890)
    c: PointOnObject(g891,g889)
    c: PointOnObject(g892,g889)
    c: PointOnObject(g893,g889)
    c: Vertical(g893)
    c: Vertical(g891)
    c: Vertical(g892)
    c: Symmetric(g887,g887,g892)
    c: Symmetric(g887,g892,g891)
    c: Symmetric(g892,g887,g893)
    c: DistanceX(g887,g887) = 19.05
    c: DistanceY(g890,g890) = 19.05
    c: Coincident(g894,g887)
    c: Coincident(g895,g894)
    c: Vertical(g895)
    c: Coincident(g896,g895)
    c: Coincident(g896,g888)
    c: Horizontal(g896)
    c: PointOnObject(g897,g889)
    c: Vertical(g897)
    c: Symmetric(g892,g893,g897)
    c: Symmetric(g893,g894,g887)
    c: Coincident(g898,g899)
    c: Coincident(g899,g900)
    c: Coincident(g900,g901)
    c: Coincident(g901,g898)
    c: Horizontal(g898)
    c: Horizontal(g900)
    c: Vertical(g899)
    c: Vertical(g901)
    c: DistanceY(g901,g901) = 14
    c: DistanceX(g898,g898) = 14
    c: Symmetric(g898,g898,g902)
    c: PointOnObject(g902,g897)
    c: DistanceY(g902,g897) = 2.525
    c: Coincident(g878,g887)
    c: Coincident(g764,g871)
    c: Coincident(g903,g904)
    c: Coincident(g904,g905)
    c: Coincident(g905,g906)
    c: Coincident(g906,g903)
    c: Horizontal(g903)
    c: Horizontal(g905)
    c: Vertical(g904)
    c: Vertical(g906)
    c: PointOnObject(g907,g905)
    c: PointOnObject(g908,g905)
    c: PointOnObject(g909,g905)
    c: Vertical(g909)
    c: Vertical(g907)
    c: Vertical(g908)
    c: Symmetric(g903,g903,g908)
    c: Symmetric(g903,g908,g907)
    c: Symmetric(g908,g903,g909)
    c: DistanceX(g903,g903) = 19.05
    c: DistanceY(g906,g906) = 19.05
    c: Coincident(g910,g903)
    c: Coincident(g911,g910)
    c: Vertical(g911)
    c: Coincident(g912,g911)
    c: Coincident(g912,g904)
    c: Horizontal(g912)
    c: Symmetric(g909,g910,g903)
    c: Coincident(g913,g910)
    c: Vertical(g914)
    c: Coincident(g915,g914)
    c: Coincident(g915,g911)
    c: Horizontal(g915)
    c: Coincident(g914,g913)
    c: Symmetric(g903,g913,g910)
    c: Coincident(g916,g913)
    c: Vertical(g917)
    c: Coincident(g918,g917)
    c: Coincident(g918,g914)
    c: Coincident(g916,g917)
    c: Horizontal(g918)
    c: Symmetric(g910,g916,g913)
    c: Vertical(g919)
    c: Symmetric(g909,g903,g919)
    c: Coincident(g920,g921)
    c: Coincident(g921,g922)
    c: Coincident(g922,g923)
    c: Coincident(g923,g920)
    c: Horizontal(g920)
    c: Horizontal(g922)
    c: Vertical(g921)
    c: Vertical(g923)
    c: DistanceX(g920,g920) = 14
    c: DistanceY(g923,g923) = 14
    c: Symmetric(g920,g920,g924)
    c: PointOnObject(g924,g919)
    c: DistanceY(g924,g919) = 2.525
    c: PointOnObject(g919,g905)
    c: Coincident(g905,g772)
    c: Coincident(g925,g926)
    c: Coincident(g926,g927)
    c: Coincident(g927,g928)
    c: Coincident(g928,g925)
    c: Horizontal(g925)
    c: Horizontal(g927)
    c: Vertical(g926)
    c: Vertical(g928)
    c: PointOnObject(g929,g927)
    c: PointOnObject(g930,g927)
    c: PointOnObject(g931,g927)
    c: Vertical(g931)
    c: Vertical(g929)
    c: Vertical(g930)
    c: Symmetric(g925,g925,g930)
    c: Symmetric(g925,g930,g929)
    c: Symmetric(g930,g925,g931)
    c: DistanceX(g925,g925) = 19.05
    c: DistanceY(g928,g928) = 19.05
    c: Coincident(g932,g925)
    c: Coincident(g933,g932)
    c: Vertical(g933)
    c: Coincident(g934,g933)
    c: Coincident(g934,g926)
    c: Horizontal(g934)
    c: Symmetric(g931,g932,g925)
    c: Coincident(g935,g932)
    c: Vertical(g936)
    c: Coincident(g937,g936)
    c: Coincident(g937,g933)
    c: Horizontal(g937)
    c: Coincident(g936,g935)
    c: Symmetric(g925,g935,g932)
    c: Coincident(g938,g939)
    c: Coincident(g939,g940)
    c: Coincident(g940,g941)
    c: Coincident(g941,g938)
    c: Horizontal(g938)
    c: Horizontal(g940)
    c: Vertical(g939)
    c: Vertical(g941)
    c: DistanceX(g938,g938) = 14
    c: DistanceY(g941,g941) = 14
    c: PointOnObject(g942,g931)
    c: Symmetric(g938,g938,g942)
    c: DistanceY(g942,g931) = 2.525
    c: Coincident(g925,g540)
    c: Coincident(g943,g944)
    c: Coincident(g944,g945)
    c: Coincident(g945,g946)
    c: Coincident(g946,g943)
    c: Horizontal(g943)
    c: Horizontal(g945)
    c: Vertical(g944)
    c: Vertical(g946)
    c: PointOnObject(g947,g945)
    c: PointOnObject(g948,g945)
    c: PointOnObject(g949,g945)
    c: Vertical(g949)
    c: Vertical(g947)
    c: Vertical(g948)
    c: Symmetric(g943,g943,g948)
    c: Symmetric(g943,g948,g947)
    c: Symmetric(g948,g943,g949)
    c: DistanceX(g943,g943) = 19.05
    c: DistanceY(g946,g946) = 19.05
    c: Coincident(g950,g951)
    c: Coincident(g951,g952)
    c: Coincident(g952,g953)
    c: Coincident(g953,g950)
    c: Horizontal(g950)
    c: Horizontal(g952)
    c: Vertical(g951)
    c: Vertical(g953)
    c: DistanceX(g950,g950) = 14
    c: DistanceY(g953,g953) = 14
    c: DistanceY(g950,g943) = 2.525
    c: DistanceX(g943,g950) = 2.525
    c: Coincident(g954,g955)
    c: Coincident(g955,g956)
    c: Coincident(g956,g957)
    c: Coincident(g957,g954)
    c: Horizontal(g954)
    c: Horizontal(g956)
    c: Vertical(g955)
    c: Vertical(g957)
    c: PointOnObject(g958,g956)
    c: PointOnObject(g959,g956)
    c: PointOnObject(g960,g956)
    c: Vertical(g960)
    c: Vertical(g958)
    c: Vertical(g959)
    c: Symmetric(g954,g954,g959)
    c: Symmetric(g954,g959,g958)
    c: Symmetric(g959,g954,g960)
    c: DistanceX(g954,g954) = 19.05
    c: DistanceY(g957,g957) = 19.05
    c: Coincident(g961,g962)
    c: Coincident(g962,g963)
    c: Coincident(g963,g964)
    c: Coincident(g964,g961)
    c: Horizontal(g961)
    c: Horizontal(g963)
    c: Vertical(g962)
    c: Vertical(g964)
    c: DistanceX(g961,g961) = 14
    c: DistanceY(g964,g964) = 14
    c: DistanceY(g961,g954) = 2.525
    c: DistanceX(g954,g961) = 2.525
    c: Coincident(g965,g966)
    c: Coincident(g966,g967)
    c: Coincident(g967,g968)
    c: Coincident(g968,g965)
    c: Horizontal(g965)
    c: Horizontal(g967)
    c: Vertical(g966)
    c: Vertical(g968)
    c: PointOnObject(g969,g967)
    c: PointOnObject(g970,g967)
    c: PointOnObject(g971,g967)
    c: Vertical(g971)
    c: Vertical(g969)
    c: Vertical(g970)
    c: Symmetric(g965,g965,g970)
    c: Symmetric(g965,g970,g969)
    c: Symmetric(g970,g965,g971)
    c: DistanceX(g965,g965) = 19.05
    c: DistanceY(g968,g968) = 19.05
    c: Coincident(g972,g973)
    c: Coincident(g973,g974)
    c: Coincident(g974,g975)
    c: Coincident(g975,g972)
    c: Horizontal(g972)
    c: Horizontal(g974)
    c: Vertical(g973)
    c: Vertical(g975)
    c: DistanceX(g972,g972) = 14
    c: DistanceY(g975,g975) = 14
    c: DistanceY(g972,g965) = 2.525
    c: DistanceX(g965,g972) = 2.525
    c: Coincident(g976,g977)
    c: Coincident(g977,g978)
    c: Coincident(g978,g979)
    c: Coincident(g979,g976)
    c: Horizontal(g976)
    c: Horizontal(g978)
    c: Vertical(g977)
    c: Vertical(g979)
    c: PointOnObject(g980,g978)
    c: PointOnObject(g981,g978)
    c: PointOnObject(g982,g978)
    c: Vertical(g982)
    c: Vertical(g980)
    c: Vertical(g981)
    c: Symmetric(g976,g976,g981)
    c: Symmetric(g976,g981,g980)
    c: Symmetric(g981,g976,g982)
    c: DistanceX(g976,g976) = 19.05
    c: DistanceY(g979,g979) = 19.05
    c: Coincident(g983,g984)
    c: Coincident(g984,g985)
    c: Coincident(g985,g986)
    c: Coincident(g986,g983)
    c: Horizontal(g983)
    c: Horizontal(g985)
    c: Vertical(g984)
    c: Vertical(g986)
    c: DistanceX(g983,g983) = 14
    c: DistanceY(g986,g986) = 14
    c: DistanceY(g983,g976) = 2.525
    c: DistanceX(g976,g983) = 2.525
    c: Coincident(g978,g954)
    c: Coincident(g965,g954)
    c: Coincident(g954,g943)
    c: DistanceY(g943,g917) = 7.1424
    c: DistanceX(g895,g943) = 7.1424
    c: Coincident(g987,g988)
    c: Coincident(g988,g989)
    c: Coincident(g989,g990)
    c: Coincident(g990,g987)
    c: Horizontal(g987)
    c: Horizontal(g989)
    c: Vertical(g988)
    c: Vertical(g990)
    c: Coincident(g991,g992)
    c: Coincident(g992,g993)
    c: Coincident(g993,g994)
    c: Coincident(g994,g991)
    c: Horizontal(g991)
    c: Horizontal(g993)
    c: Vertical(g992)
    c: Vertical(g994)
    c: Coincident(g995,g996)
    c: Coincident(g996,g997)
    c: Coincident(g997,g998)
    c: Coincident(g998,g995)
    c: Horizontal(g995)
    c: Horizontal(g997)
    c: Vertical(g996)
    c: Vertical(g998)
    c: Coincident(g999,g1000)
    c: Coincident(g1000,g1001)
    c: Coincident(g1001,g1002)
    c: Coincident(g1002,g999)
    c: Horizontal(g999)
    c: Horizontal(g1001)
    c: Vertical(g1000)
    c: Vertical(g1002)
    c: DistanceX(g684,g987) = 0
    c: PointOnObject(g1003,g987)
    c: PointOnObject(g1003,g989)
    c: Vertical(g1003)
    c: Symmetric(g987,g987,g1003)
